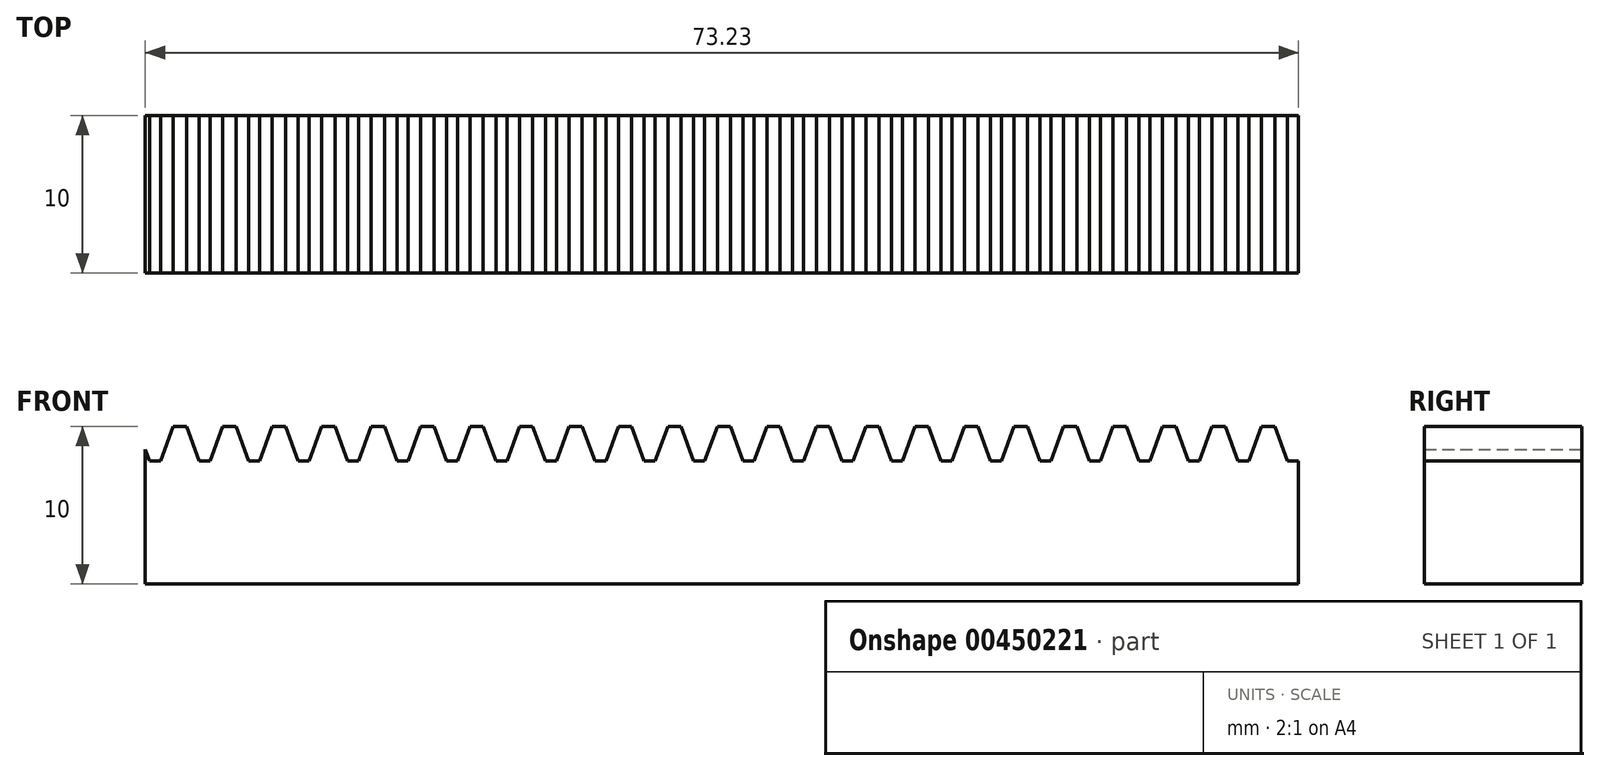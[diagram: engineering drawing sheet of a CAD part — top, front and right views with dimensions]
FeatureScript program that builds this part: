
annotation { "Feature Type Name" : "Feature", "Feature Type Description" : "" }
export const myFeature = defineFeature(function(context is Context, id is Id, definition is map)
    precondition{}
    {
        {
            var Q0;
            Q0=qCreatedBy(makeId("Front.planeOp"),FACE);
            var sketch = newSketch(context, id + "F0", { "sketchPlane" : qUnion([Q0])});
            skLineSegment(sketch, "E0", {"start": v(245.18, 2.55) * mm, "end": v(245.77, 2.55) * mm});
            skLineSegment(sketch, "E1", {"start": v(245.77, 2.55) * mm, "end": v(245.77, -5.25) * mm});
            skLineSegment(sketch, "E2", {"start": v(245.77, -5.25) * mm, "end": v(-50.4, -5.25) * mm});
            skLineSegment(sketch, "E3", {"start": v(244.38, 4.75) * mm, "end": v(245.18, 2.55) * mm});
            skLineSegment(sketch, "E4", {"start": v(242.74, 2.55) * mm, "end": v(243.54, 4.75) * mm});
            skLineSegment(sketch, "E5", {"start": v(242.04, 2.55) * mm, "end": v(242.74, 2.55) * mm});
            skLineSegment(sketch, "E6", {"start": v(243.54, 4.75) * mm, "end": v(244.38, 4.75) * mm});
            skLineSegment(sketch, "E7", {"start": v(241.24, 4.75) * mm, "end": v(242.04, 2.55) * mm});
            skLineSegment(sketch, "E8", {"start": v(240.4, 4.75) * mm, "end": v(241.24, 4.75) * mm});
            skLineSegment(sketch, "E9", {"start": v(239.6, 2.55) * mm, "end": v(240.4, 4.75) * mm});
            skLineSegment(sketch, "E10", {"start": v(238.9, 2.55) * mm, "end": v(239.6, 2.55) * mm});
            skLineSegment(sketch, "E11", {"start": v(238.1, 4.75) * mm, "end": v(238.9, 2.55) * mm});
            skLineSegment(sketch, "E12", {"start": v(237.25, 4.75) * mm, "end": v(238.1, 4.75) * mm});
            skLineSegment(sketch, "E13", {"start": v(236.45, 2.55) * mm, "end": v(237.25, 4.75) * mm});
            skLineSegment(sketch, "E14", {"start": v(235.76, 2.55) * mm, "end": v(236.45, 2.55) * mm});
            skLineSegment(sketch, "E15", {"start": v(234.96, 4.75) * mm, "end": v(235.76, 2.55) * mm});
            skLineSegment(sketch, "E16", {"start": v(234.11, 4.75) * mm, "end": v(234.96, 4.75) * mm});
            skLineSegment(sketch, "E17", {"start": v(233.31, 2.55) * mm, "end": v(234.11, 4.75) * mm});
            skLineSegment(sketch, "E18", {"start": v(232.62, 2.55) * mm, "end": v(233.31, 2.55) * mm});
            skLineSegment(sketch, "E19", {"start": v(231.81, 4.75) * mm, "end": v(232.62, 2.55) * mm});
            skLineSegment(sketch, "E20", {"start": v(230.97, 4.75) * mm, "end": v(231.81, 4.75) * mm});
            skLineSegment(sketch, "E21", {"start": v(230.17, 2.55) * mm, "end": v(230.97, 4.75) * mm});
            skLineSegment(sketch, "E22", {"start": v(229.47, 2.55) * mm, "end": v(230.17, 2.55) * mm});
            skLineSegment(sketch, "E23", {"start": v(228.67, 4.75) * mm, "end": v(229.47, 2.55) * mm});
            skLineSegment(sketch, "E24", {"start": v(227.83, 4.75) * mm, "end": v(228.67, 4.75) * mm});
            skLineSegment(sketch, "E25", {"start": v(227.03, 2.55) * mm, "end": v(227.83, 4.75) * mm});
            skLineSegment(sketch, "E26", {"start": v(226.33, 2.55) * mm, "end": v(227.03, 2.55) * mm});
            skLineSegment(sketch, "E27", {"start": v(225.53, 4.75) * mm, "end": v(226.33, 2.55) * mm});
            skLineSegment(sketch, "E28", {"start": v(224.69, 4.75) * mm, "end": v(225.53, 4.75) * mm});
            skLineSegment(sketch, "E29", {"start": v(223.89, 2.55) * mm, "end": v(224.69, 4.75) * mm});
            skLineSegment(sketch, "E30", {"start": v(223.2, 2.55) * mm, "end": v(223.89, 2.55) * mm});
            skLineSegment(sketch, "E31", {"start": v(222.39, 4.75) * mm, "end": v(223.2, 2.55) * mm});
            skLineSegment(sketch, "E32", {"start": v(221.55, 4.75) * mm, "end": v(222.39, 4.75) * mm});
            skLineSegment(sketch, "E33", {"start": v(220.75, 2.55) * mm, "end": v(221.55, 4.75) * mm});
            skLineSegment(sketch, "E34", {"start": v(220.05, 2.55) * mm, "end": v(220.75, 2.55) * mm});
            skLineSegment(sketch, "E35", {"start": v(219.25, 4.75) * mm, "end": v(220.05, 2.55) * mm});
            skLineSegment(sketch, "E36", {"start": v(218.4, 4.75) * mm, "end": v(219.25, 4.75) * mm});
            skLineSegment(sketch, "E37", {"start": v(217.6, 2.55) * mm, "end": v(218.4, 4.75) * mm});
            skLineSegment(sketch, "E38", {"start": v(216.9, 2.55) * mm, "end": v(217.6, 2.55) * mm});
            skLineSegment(sketch, "E39", {"start": v(216.1, 4.75) * mm, "end": v(216.9, 2.55) * mm});
            skLineSegment(sketch, "E40", {"start": v(215.26, 4.75) * mm, "end": v(216.1, 4.75) * mm});
            skLineSegment(sketch, "E41", {"start": v(214.46, 2.55) * mm, "end": v(215.26, 4.75) * mm});
            skLineSegment(sketch, "E42", {"start": v(213.77, 2.55) * mm, "end": v(214.46, 2.55) * mm});
            skLineSegment(sketch, "E43", {"start": v(212.96, 4.75) * mm, "end": v(213.77, 2.55) * mm});
            skLineSegment(sketch, "E44", {"start": v(212.12, 4.75) * mm, "end": v(212.96, 4.75) * mm});
            skLineSegment(sketch, "E45", {"start": v(211.32, 2.55) * mm, "end": v(212.12, 4.75) * mm});
            skLineSegment(sketch, "E46", {"start": v(210.62, 2.55) * mm, "end": v(211.32, 2.55) * mm});
            skLineSegment(sketch, "E47", {"start": v(209.82, 4.75) * mm, "end": v(210.62, 2.55) * mm});
            skLineSegment(sketch, "E48", {"start": v(208.98, 4.75) * mm, "end": v(209.82, 4.75) * mm});
            skLineSegment(sketch, "E49", {"start": v(208.18, 2.55) * mm, "end": v(208.98, 4.75) * mm});
            skLineSegment(sketch, "E50", {"start": v(207.48, 2.55) * mm, "end": v(208.18, 2.55) * mm});
            skLineSegment(sketch, "E51", {"start": v(206.68, 4.75) * mm, "end": v(207.48, 2.55) * mm});
            skLineSegment(sketch, "E52", {"start": v(205.84, 4.75) * mm, "end": v(206.68, 4.75) * mm});
            skLineSegment(sketch, "E53", {"start": v(205.04, 2.55) * mm, "end": v(205.84, 4.75) * mm});
            skLineSegment(sketch, "E54", {"start": v(204.34, 2.55) * mm, "end": v(205.04, 2.55) * mm});
            skLineSegment(sketch, "E55", {"start": v(203.54, 4.75) * mm, "end": v(204.34, 2.55) * mm});
            skLineSegment(sketch, "E56", {"start": v(202.7, 4.75) * mm, "end": v(203.54, 4.75) * mm});
            skLineSegment(sketch, "E57", {"start": v(201.9, 2.55) * mm, "end": v(202.7, 4.75) * mm});
            skLineSegment(sketch, "E58", {"start": v(201.2, 2.55) * mm, "end": v(201.9, 2.55) * mm});
            skLineSegment(sketch, "E59", {"start": v(200.4, 4.75) * mm, "end": v(201.2, 2.55) * mm});
            skLineSegment(sketch, "E60", {"start": v(199.56, 4.75) * mm, "end": v(200.4, 4.75) * mm});
            skLineSegment(sketch, "E61", {"start": v(198.75, 2.55) * mm, "end": v(199.56, 4.75) * mm});
            skLineSegment(sketch, "E62", {"start": v(198.06, 2.55) * mm, "end": v(198.75, 2.55) * mm});
            skLineSegment(sketch, "E63", {"start": v(197.26, 4.75) * mm, "end": v(198.06, 2.55) * mm});
            skLineSegment(sketch, "E64", {"start": v(196.41, 4.75) * mm, "end": v(197.26, 4.75) * mm});
            skLineSegment(sketch, "E65", {"start": v(195.61, 2.55) * mm, "end": v(196.41, 4.75) * mm});
            skLineSegment(sketch, "E66", {"start": v(194.92, 2.55) * mm, "end": v(195.61, 2.55) * mm});
            skLineSegment(sketch, "E67", {"start": v(194.12, 4.75) * mm, "end": v(194.92, 2.55) * mm});
            skLineSegment(sketch, "E68", {"start": v(193.27, 4.75) * mm, "end": v(194.12, 4.75) * mm});
            skLineSegment(sketch, "E69", {"start": v(192.47, 2.55) * mm, "end": v(193.27, 4.75) * mm});
            skLineSegment(sketch, "E70", {"start": v(191.77, 2.55) * mm, "end": v(192.47, 2.55) * mm});
            skLineSegment(sketch, "E71", {"start": v(190.97, 4.75) * mm, "end": v(191.77, 2.55) * mm});
            skLineSegment(sketch, "E72", {"start": v(190.13, 4.75) * mm, "end": v(190.97, 4.75) * mm});
            skLineSegment(sketch, "E73", {"start": v(189.33, 2.55) * mm, "end": v(190.13, 4.75) * mm});
            skLineSegment(sketch, "E74", {"start": v(188.63, 2.55) * mm, "end": v(189.33, 2.55) * mm});
            skLineSegment(sketch, "E75", {"start": v(187.83, 4.75) * mm, "end": v(188.63, 2.55) * mm});
            skLineSegment(sketch, "E76", {"start": v(186.99, 4.75) * mm, "end": v(187.83, 4.75) * mm});
            skLineSegment(sketch, "E77", {"start": v(186.19, 2.55) * mm, "end": v(186.99, 4.75) * mm});
            skLineSegment(sketch, "E78", {"start": v(185.5, 2.55) * mm, "end": v(186.19, 2.55) * mm});
            skLineSegment(sketch, "E79", {"start": v(184.7, 4.75) * mm, "end": v(185.5, 2.55) * mm});
            skLineSegment(sketch, "E80", {"start": v(183.85, 4.75) * mm, "end": v(184.7, 4.75) * mm});
            skLineSegment(sketch, "E81", {"start": v(183.05, 2.55) * mm, "end": v(183.85, 4.75) * mm});
            skLineSegment(sketch, "E82", {"start": v(182.35, 2.55) * mm, "end": v(183.05, 2.55) * mm});
            skLineSegment(sketch, "E83", {"start": v(181.55, 4.75) * mm, "end": v(182.35, 2.55) * mm});
            skLineSegment(sketch, "E84", {"start": v(180.7, 4.75) * mm, "end": v(181.55, 4.75) * mm});
            skLineSegment(sketch, "E85", {"start": v(179.9, 2.55) * mm, "end": v(180.7, 4.75) * mm});
            skLineSegment(sketch, "E86", {"start": v(179.2, 2.55) * mm, "end": v(179.9, 2.55) * mm});
            skLineSegment(sketch, "E87", {"start": v(178.4, 4.75) * mm, "end": v(179.2, 2.55) * mm});
            skLineSegment(sketch, "E88", {"start": v(177.56, 4.75) * mm, "end": v(178.4, 4.75) * mm});
            skLineSegment(sketch, "E89", {"start": v(176.76, 2.55) * mm, "end": v(177.56, 4.75) * mm});
            skLineSegment(sketch, "E90", {"start": v(176.07, 2.55) * mm, "end": v(176.76, 2.55) * mm});
            skLineSegment(sketch, "E91", {"start": v(175.27, 4.75) * mm, "end": v(176.07, 2.55) * mm});
            skLineSegment(sketch, "E92", {"start": v(174.42, 4.75) * mm, "end": v(175.27, 4.75) * mm});
            skLineSegment(sketch, "E93", {"start": v(173.62, 2.55) * mm, "end": v(174.42, 4.75) * mm});
            skLineSegment(sketch, "E94", {"start": v(172.93, 2.55) * mm, "end": v(173.62, 2.55) * mm});
            skLineSegment(sketch, "E95", {"start": v(172.12, 4.75) * mm, "end": v(172.93, 2.55) * mm});
            skLineSegment(sketch, "E96", {"start": v(171.28, 4.75) * mm, "end": v(172.12, 4.75) * mm});
            skLineSegment(sketch, "E97", {"start": v(170.48, 2.55) * mm, "end": v(171.28, 4.75) * mm});
            skLineSegment(sketch, "E98", {"start": v(169.78, 2.55) * mm, "end": v(170.48, 2.55) * mm});
            skLineSegment(sketch, "E99", {"start": v(168.98, 4.75) * mm, "end": v(169.78, 2.55) * mm});
            skLineSegment(sketch, "E100", {"start": v(168.14, 4.75) * mm, "end": v(168.98, 4.75) * mm});
            skLineSegment(sketch, "E101", {"start": v(167.34, 2.55) * mm, "end": v(168.14, 4.75) * mm});
            skLineSegment(sketch, "E102", {"start": v(166.64, 2.55) * mm, "end": v(167.34, 2.55) * mm});
            skLineSegment(sketch, "E103", {"start": v(165.84, 4.75) * mm, "end": v(166.64, 2.55) * mm});
            skLineSegment(sketch, "E104", {"start": v(165, 4.75) * mm, "end": v(165.84, 4.75) * mm});
            skLineSegment(sketch, "E105", {"start": v(164.2, 2.55) * mm, "end": v(165, 4.75) * mm});
            skLineSegment(sketch, "E106", {"start": v(163.5, 2.55) * mm, "end": v(164.2, 2.55) * mm});
            skLineSegment(sketch, "E107", {"start": v(162.7, 4.75) * mm, "end": v(163.5, 2.55) * mm});
            skLineSegment(sketch, "E108", {"start": v(161.86, 4.75) * mm, "end": v(162.7, 4.75) * mm});
            skLineSegment(sketch, "E109", {"start": v(161.06, 2.55) * mm, "end": v(161.86, 4.75) * mm});
            skLineSegment(sketch, "E110", {"start": v(160.36, 2.55) * mm, "end": v(161.06, 2.55) * mm});
            skLineSegment(sketch, "E111", {"start": v(159.56, 4.75) * mm, "end": v(160.36, 2.55) * mm});
            skLineSegment(sketch, "E112", {"start": v(158.72, 4.75) * mm, "end": v(159.56, 4.75) * mm});
            skLineSegment(sketch, "E113", {"start": v(157.91, 2.55) * mm, "end": v(158.72, 4.75) * mm});
            skLineSegment(sketch, "E114", {"start": v(157.22, 2.55) * mm, "end": v(157.91, 2.55) * mm});
            skLineSegment(sketch, "E115", {"start": v(156.42, 4.75) * mm, "end": v(157.22, 2.55) * mm});
            skLineSegment(sketch, "E116", {"start": v(155.57, 4.75) * mm, "end": v(156.42, 4.75) * mm});
            skLineSegment(sketch, "E117", {"start": v(154.77, 2.55) * mm, "end": v(155.57, 4.75) * mm});
            skLineSegment(sketch, "E118", {"start": v(154.08, 2.55) * mm, "end": v(154.77, 2.55) * mm});
            skLineSegment(sketch, "E119", {"start": v(153.27, 4.75) * mm, "end": v(154.08, 2.55) * mm});
            skLineSegment(sketch, "E120", {"start": v(152.43, 4.75) * mm, "end": v(153.27, 4.75) * mm});
            skLineSegment(sketch, "E121", {"start": v(151.63, 2.55) * mm, "end": v(152.43, 4.75) * mm});
            skLineSegment(sketch, "E122", {"start": v(150.93, 2.55) * mm, "end": v(151.63, 2.55) * mm});
            skLineSegment(sketch, "E123", {"start": v(150.13, 4.75) * mm, "end": v(150.93, 2.55) * mm});
            skLineSegment(sketch, "E124", {"start": v(149.3, 4.75) * mm, "end": v(150.13, 4.75) * mm});
            skLineSegment(sketch, "E125", {"start": v(148.49, 2.55) * mm, "end": v(149.3, 4.75) * mm});
            skLineSegment(sketch, "E126", {"start": v(147.8, 2.55) * mm, "end": v(148.49, 2.55) * mm});
            skLineSegment(sketch, "E127", {"start": v(147, 4.75) * mm, "end": v(147.8, 2.55) * mm});
            skLineSegment(sketch, "E128", {"start": v(146.15, 4.75) * mm, "end": v(147, 4.75) * mm});
            skLineSegment(sketch, "E129", {"start": v(145.35, 2.55) * mm, "end": v(146.15, 4.75) * mm});
            skLineSegment(sketch, "E130", {"start": v(144.65, 2.55) * mm, "end": v(145.35, 2.55) * mm});
            skLineSegment(sketch, "E131", {"start": v(143.85, 4.75) * mm, "end": v(144.65, 2.55) * mm});
            skLineSegment(sketch, "E132", {"start": v(143, 4.75) * mm, "end": v(143.85, 4.75) * mm});
            skLineSegment(sketch, "E133", {"start": v(142.2, 2.55) * mm, "end": v(143, 4.75) * mm});
            skLineSegment(sketch, "E134", {"start": v(141.5, 2.55) * mm, "end": v(142.2, 2.55) * mm});
            skLineSegment(sketch, "E135", {"start": v(140.7, 4.75) * mm, "end": v(141.5, 2.55) * mm});
            skLineSegment(sketch, "E136", {"start": v(139.87, 4.75) * mm, "end": v(140.7, 4.75) * mm});
            skLineSegment(sketch, "E137", {"start": v(139.06, 2.55) * mm, "end": v(139.87, 4.75) * mm});
            skLineSegment(sketch, "E138", {"start": v(138.37, 2.55) * mm, "end": v(139.06, 2.55) * mm});
            skLineSegment(sketch, "E139", {"start": v(137.57, 4.75) * mm, "end": v(138.37, 2.55) * mm});
            skLineSegment(sketch, "E140", {"start": v(136.72, 4.75) * mm, "end": v(137.57, 4.75) * mm});
            skLineSegment(sketch, "E141", {"start": v(135.92, 2.55) * mm, "end": v(136.72, 4.75) * mm});
            skLineSegment(sketch, "E142", {"start": v(135.23, 2.55) * mm, "end": v(135.92, 2.55) * mm});
            skLineSegment(sketch, "E143", {"start": v(134.43, 4.75) * mm, "end": v(135.23, 2.55) * mm});
            skLineSegment(sketch, "E144", {"start": v(133.58, 4.75) * mm, "end": v(134.43, 4.75) * mm});
            skLineSegment(sketch, "E145", {"start": v(132.78, 2.55) * mm, "end": v(133.58, 4.75) * mm});
            skLineSegment(sketch, "E146", {"start": v(132.08, 2.55) * mm, "end": v(132.78, 2.55) * mm});
            skLineSegment(sketch, "E147", {"start": v(131.28, 4.75) * mm, "end": v(132.08, 2.55) * mm});
            skLineSegment(sketch, "E148", {"start": v(130.44, 4.75) * mm, "end": v(131.28, 4.75) * mm});
            skLineSegment(sketch, "E149", {"start": v(129.64, 2.55) * mm, "end": v(130.44, 4.75) * mm});
            skLineSegment(sketch, "E150", {"start": v(128.94, 2.55) * mm, "end": v(129.64, 2.55) * mm});
            skLineSegment(sketch, "E151", {"start": v(128.14, 4.75) * mm, "end": v(128.94, 2.55) * mm});
            skLineSegment(sketch, "E152", {"start": v(127.3, 4.75) * mm, "end": v(128.14, 4.75) * mm});
            skLineSegment(sketch, "E153", {"start": v(126.5, 2.55) * mm, "end": v(127.3, 4.75) * mm});
            skLineSegment(sketch, "E154", {"start": v(125.8, 2.55) * mm, "end": v(126.5, 2.55) * mm});
            skLineSegment(sketch, "E155", {"start": v(125, 4.75) * mm, "end": v(125.8, 2.55) * mm});
            skLineSegment(sketch, "E156", {"start": v(124.16, 4.75) * mm, "end": v(125, 4.75) * mm});
            skLineSegment(sketch, "E157", {"start": v(123.36, 2.55) * mm, "end": v(124.16, 4.75) * mm});
            skLineSegment(sketch, "E158", {"start": v(122.66, 2.55) * mm, "end": v(123.36, 2.55) * mm});
            skLineSegment(sketch, "E159", {"start": v(121.86, 4.75) * mm, "end": v(122.66, 2.55) * mm});
            skLineSegment(sketch, "E160", {"start": v(121.02, 4.75) * mm, "end": v(121.86, 4.75) * mm});
            skLineSegment(sketch, "E161", {"start": v(120.22, 2.55) * mm, "end": v(121.02, 4.75) * mm});
            skLineSegment(sketch, "E162", {"start": v(119.52, 2.55) * mm, "end": v(120.22, 2.55) * mm});
            skLineSegment(sketch, "E163", {"start": v(118.72, 4.75) * mm, "end": v(119.52, 2.55) * mm});
            skLineSegment(sketch, "E164", {"start": v(117.87, 4.75) * mm, "end": v(118.72, 4.75) * mm});
            skLineSegment(sketch, "E165", {"start": v(117.07, 2.55) * mm, "end": v(117.87, 4.75) * mm});
            skLineSegment(sketch, "E166", {"start": v(116.38, 2.55) * mm, "end": v(117.07, 2.55) * mm});
            skLineSegment(sketch, "E167", {"start": v(115.58, 4.75) * mm, "end": v(116.38, 2.55) * mm});
            skLineSegment(sketch, "E168", {"start": v(114.73, 4.75) * mm, "end": v(115.58, 4.75) * mm});
            skLineSegment(sketch, "E169", {"start": v(113.93, 2.55) * mm, "end": v(114.73, 4.75) * mm});
            skLineSegment(sketch, "E170", {"start": v(113.23, 2.55) * mm, "end": v(113.93, 2.55) * mm});
            skLineSegment(sketch, "E171", {"start": v(112.43, 4.75) * mm, "end": v(113.23, 2.55) * mm});
            skLineSegment(sketch, "E172", {"start": v(111.6, 4.75) * mm, "end": v(112.43, 4.75) * mm});
            skLineSegment(sketch, "E173", {"start": v(110.8, 2.55) * mm, "end": v(111.6, 4.75) * mm});
            skLineSegment(sketch, "E174", {"start": v(110.1, 2.55) * mm, "end": v(110.8, 2.55) * mm});
            skLineSegment(sketch, "E175", {"start": v(109.3, 4.75) * mm, "end": v(110.1, 2.55) * mm});
            skLineSegment(sketch, "E176", {"start": v(108.45, 4.75) * mm, "end": v(109.3, 4.75) * mm});
            skLineSegment(sketch, "E177", {"start": v(107.65, 2.55) * mm, "end": v(108.45, 4.75) * mm});
            skLineSegment(sketch, "E178", {"start": v(106.95, 2.55) * mm, "end": v(107.65, 2.55) * mm});
            skLineSegment(sketch, "E179", {"start": v(106.15, 4.75) * mm, "end": v(106.95, 2.55) * mm});
            skLineSegment(sketch, "E180", {"start": v(105.3, 4.75) * mm, "end": v(106.15, 4.75) * mm});
            skLineSegment(sketch, "E181", {"start": v(104.5, 2.55) * mm, "end": v(105.3, 4.75) * mm});
            skLineSegment(sketch, "E182", {"start": v(103.81, 2.55) * mm, "end": v(104.5, 2.55) * mm});
            skLineSegment(sketch, "E183", {"start": v(103, 4.75) * mm, "end": v(103.81, 2.55) * mm});
            skLineSegment(sketch, "E184", {"start": v(102.17, 4.75) * mm, "end": v(103, 4.75) * mm});
            skLineSegment(sketch, "E185", {"start": v(101.37, 2.55) * mm, "end": v(102.17, 4.75) * mm});
            skLineSegment(sketch, "E186", {"start": v(100.67, 2.55) * mm, "end": v(101.37, 2.55) * mm});
            skLineSegment(sketch, "E187", {"start": v(99.87, 4.75) * mm, "end": v(100.67, 2.55) * mm});
            skLineSegment(sketch, "E188", {"start": v(99.02, 4.75) * mm, "end": v(99.87, 4.75) * mm});
            skLineSegment(sketch, "E189", {"start": v(98.22, 2.55) * mm, "end": v(99.02, 4.75) * mm});
            skLineSegment(sketch, "E190", {"start": v(97.53, 2.55) * mm, "end": v(98.22, 2.55) * mm});
            skLineSegment(sketch, "E191", {"start": v(96.73, 4.75) * mm, "end": v(97.53, 2.55) * mm});
            skLineSegment(sketch, "E192", {"start": v(95.88, 4.75) * mm, "end": v(96.73, 4.75) * mm});
            skLineSegment(sketch, "E193", {"start": v(95.08, 2.55) * mm, "end": v(95.88, 4.75) * mm});
            skLineSegment(sketch, "E194", {"start": v(94.39, 2.55) * mm, "end": v(95.08, 2.55) * mm});
            skLineSegment(sketch, "E195", {"start": v(93.58, 4.75) * mm, "end": v(94.39, 2.55) * mm});
            skLineSegment(sketch, "E196", {"start": v(92.74, 4.75) * mm, "end": v(93.58, 4.75) * mm});
            skLineSegment(sketch, "E197", {"start": v(91.94, 2.55) * mm, "end": v(92.74, 4.75) * mm});
            skLineSegment(sketch, "E198", {"start": v(91.24, 2.55) * mm, "end": v(91.94, 2.55) * mm});
            skLineSegment(sketch, "E199", {"start": v(90.44, 4.75) * mm, "end": v(91.24, 2.55) * mm});
            skLineSegment(sketch, "E200", {"start": v(89.6, 4.75) * mm, "end": v(90.44, 4.75) * mm});
            skLineSegment(sketch, "E201", {"start": v(88.8, 2.55) * mm, "end": v(89.6, 4.75) * mm});
            skLineSegment(sketch, "E202", {"start": v(88.1, 2.55) * mm, "end": v(88.8, 2.55) * mm});
            skLineSegment(sketch, "E203", {"start": v(87.3, 4.75) * mm, "end": v(88.1, 2.55) * mm});
            skLineSegment(sketch, "E204", {"start": v(86.46, 4.75) * mm, "end": v(87.3, 4.75) * mm});
            skLineSegment(sketch, "E205", {"start": v(85.66, 2.55) * mm, "end": v(86.46, 4.75) * mm});
            skLineSegment(sketch, "E206", {"start": v(84.96, 2.55) * mm, "end": v(85.66, 2.55) * mm});
            skLineSegment(sketch, "E207", {"start": v(84.16, 4.75) * mm, "end": v(84.96, 2.55) * mm});
            skLineSegment(sketch, "E208", {"start": v(83.32, 4.75) * mm, "end": v(84.16, 4.75) * mm});
            skLineSegment(sketch, "E209", {"start": v(82.52, 2.55) * mm, "end": v(83.32, 4.75) * mm});
            skLineSegment(sketch, "E210", {"start": v(81.82, 2.55) * mm, "end": v(82.52, 2.55) * mm});
            skLineSegment(sketch, "E211", {"start": v(81.02, 4.75) * mm, "end": v(81.82, 2.55) * mm});
            skLineSegment(sketch, "E212", {"start": v(80.18, 4.75) * mm, "end": v(81.02, 4.75) * mm});
            skLineSegment(sketch, "E213", {"start": v(79.37, 2.55) * mm, "end": v(80.18, 4.75) * mm});
            skLineSegment(sketch, "E214", {"start": v(78.68, 2.55) * mm, "end": v(79.37, 2.55) * mm});
            skLineSegment(sketch, "E215", {"start": v(77.88, 4.75) * mm, "end": v(78.68, 2.55) * mm});
            skLineSegment(sketch, "E216", {"start": v(77.03, 4.75) * mm, "end": v(77.88, 4.75) * mm});
            skLineSegment(sketch, "E217", {"start": v(76.23, 2.55) * mm, "end": v(77.03, 4.75) * mm});
            skLineSegment(sketch, "E218", {"start": v(75.54, 2.55) * mm, "end": v(76.23, 2.55) * mm});
            skLineSegment(sketch, "E219", {"start": v(74.73, 4.75) * mm, "end": v(75.54, 2.55) * mm});
            skLineSegment(sketch, "E220", {"start": v(73.9, 4.75) * mm, "end": v(74.73, 4.75) * mm});
            skLineSegment(sketch, "E221", {"start": v(73.1, 2.55) * mm, "end": v(73.9, 4.75) * mm});
            skLineSegment(sketch, "E222", {"start": v(72.4, 2.55) * mm, "end": v(73.1, 2.55) * mm});
            skLineSegment(sketch, "E223", {"start": v(71.6, 4.75) * mm, "end": v(72.4, 2.55) * mm});
            skLineSegment(sketch, "E224", {"start": v(70.75, 4.75) * mm, "end": v(71.6, 4.75) * mm});
            skLineSegment(sketch, "E225", {"start": v(69.95, 2.55) * mm, "end": v(70.75, 4.75) * mm});
            skLineSegment(sketch, "E226", {"start": v(69.25, 2.55) * mm, "end": v(69.95, 2.55) * mm});
            skLineSegment(sketch, "E227", {"start": v(68.45, 4.75) * mm, "end": v(69.25, 2.55) * mm});
            skLineSegment(sketch, "E228", {"start": v(67.6, 4.75) * mm, "end": v(68.45, 4.75) * mm});
            skLineSegment(sketch, "E229", {"start": v(66.8, 2.55) * mm, "end": v(67.6, 4.75) * mm});
            skLineSegment(sketch, "E230", {"start": v(66.11, 2.55) * mm, "end": v(66.8, 2.55) * mm});
            skLineSegment(sketch, "E231", {"start": v(65.31, 4.75) * mm, "end": v(66.11, 2.55) * mm});
            skLineSegment(sketch, "E232", {"start": v(64.47, 4.75) * mm, "end": v(65.31, 4.75) * mm});
            skLineSegment(sketch, "E233", {"start": v(63.67, 2.55) * mm, "end": v(64.47, 4.75) * mm});
            skLineSegment(sketch, "E234", {"start": v(62.97, 2.55) * mm, "end": v(63.67, 2.55) * mm});
            skLineSegment(sketch, "E235", {"start": v(62.17, 4.75) * mm, "end": v(62.97, 2.55) * mm});
            skLineSegment(sketch, "E236", {"start": v(61.33, 4.75) * mm, "end": v(62.17, 4.75) * mm});
            skLineSegment(sketch, "E237", {"start": v(60.53, 2.55) * mm, "end": v(61.33, 4.75) * mm});
            skLineSegment(sketch, "E238", {"start": v(59.83, 2.55) * mm, "end": v(60.53, 2.55) * mm});
            skLineSegment(sketch, "E239", {"start": v(59.03, 4.75) * mm, "end": v(59.83, 2.55) * mm});
            skLineSegment(sketch, "E240", {"start": v(58.18, 4.75) * mm, "end": v(59.03, 4.75) * mm});
            skLineSegment(sketch, "E241", {"start": v(57.38, 2.55) * mm, "end": v(58.18, 4.75) * mm});
            skLineSegment(sketch, "E242", {"start": v(56.69, 2.55) * mm, "end": v(57.38, 2.55) * mm});
            skLineSegment(sketch, "E243", {"start": v(55.89, 4.75) * mm, "end": v(56.69, 2.55) * mm});
            skLineSegment(sketch, "E244", {"start": v(55.04, 4.75) * mm, "end": v(55.89, 4.75) * mm});
            skLineSegment(sketch, "E245", {"start": v(54.24, 2.55) * mm, "end": v(55.04, 4.75) * mm});
            skLineSegment(sketch, "E246", {"start": v(53.54, 2.55) * mm, "end": v(54.24, 2.55) * mm});
            skLineSegment(sketch, "E247", {"start": v(52.74, 4.75) * mm, "end": v(53.54, 2.55) * mm});
            skLineSegment(sketch, "E248", {"start": v(51.9, 4.75) * mm, "end": v(52.74, 4.75) * mm});
            skLineSegment(sketch, "E249", {"start": v(51.1, 2.55) * mm, "end": v(51.9, 4.75) * mm});
            skLineSegment(sketch, "E250", {"start": v(50.4, 2.55) * mm, "end": v(51.1, 2.55) * mm});
            skLineSegment(sketch, "E251", {"start": v(49.6, 4.75) * mm, "end": v(50.4, 2.55) * mm});
            skLineSegment(sketch, "E252", {"start": v(48.76, 4.75) * mm, "end": v(49.6, 4.75) * mm});
            skLineSegment(sketch, "E253", {"start": v(47.96, 2.55) * mm, "end": v(48.76, 4.75) * mm});
            skLineSegment(sketch, "E254", {"start": v(47.26, 2.55) * mm, "end": v(47.96, 2.55) * mm});
            skLineSegment(sketch, "E255", {"start": v(46.46, 4.75) * mm, "end": v(47.26, 2.55) * mm});
            skLineSegment(sketch, "E256", {"start": v(45.62, 4.75) * mm, "end": v(46.46, 4.75) * mm});
            skLineSegment(sketch, "E257", {"start": v(44.82, 2.55) * mm, "end": v(45.62, 4.75) * mm});
            skLineSegment(sketch, "E258", {"start": v(44.12, 2.55) * mm, "end": v(44.82, 2.55) * mm});
            skLineSegment(sketch, "E259", {"start": v(43.32, 4.75) * mm, "end": v(44.12, 2.55) * mm});
            skLineSegment(sketch, "E260", {"start": v(42.48, 4.75) * mm, "end": v(43.32, 4.75) * mm});
            skLineSegment(sketch, "E261", {"start": v(41.68, 2.55) * mm, "end": v(42.48, 4.75) * mm});
            skLineSegment(sketch, "E262", {"start": v(40.98, 2.55) * mm, "end": v(41.68, 2.55) * mm});
            skLineSegment(sketch, "E263", {"start": v(40.18, 4.75) * mm, "end": v(40.98, 2.55) * mm});
            skLineSegment(sketch, "E264", {"start": v(39.33, 4.75) * mm, "end": v(40.18, 4.75) * mm});
            skLineSegment(sketch, "E265", {"start": v(38.53, 2.55) * mm, "end": v(39.33, 4.75) * mm});
            skLineSegment(sketch, "E266", {"start": v(37.84, 2.55) * mm, "end": v(38.53, 2.55) * mm});
            skLineSegment(sketch, "E267", {"start": v(37.04, 4.75) * mm, "end": v(37.84, 2.55) * mm});
            skLineSegment(sketch, "E268", {"start": v(36.2, 4.75) * mm, "end": v(37.04, 4.75) * mm});
            skLineSegment(sketch, "E269", {"start": v(35.4, 2.55) * mm, "end": v(36.2, 4.75) * mm});
            skLineSegment(sketch, "E270", {"start": v(34.7, 2.55) * mm, "end": v(35.4, 2.55) * mm});
            skLineSegment(sketch, "E271", {"start": v(33.9, 4.75) * mm, "end": v(34.7, 2.55) * mm});
            skLineSegment(sketch, "E272", {"start": v(33.05, 4.75) * mm, "end": v(33.9, 4.75) * mm});
            skLineSegment(sketch, "E273", {"start": v(32.25, 2.55) * mm, "end": v(33.05, 4.75) * mm});
            skLineSegment(sketch, "E274", {"start": v(31.55, 2.55) * mm, "end": v(32.25, 2.55) * mm});
            skLineSegment(sketch, "E275", {"start": v(30.75, 4.75) * mm, "end": v(31.55, 2.55) * mm});
            skLineSegment(sketch, "E276", {"start": v(29.9, 4.75) * mm, "end": v(30.75, 4.75) * mm});
            skLineSegment(sketch, "E277", {"start": v(29.1, 2.55) * mm, "end": v(29.9, 4.75) * mm});
            skLineSegment(sketch, "E278", {"start": v(28.41, 2.55) * mm, "end": v(29.1, 2.55) * mm});
            skLineSegment(sketch, "E279", {"start": v(27.61, 4.75) * mm, "end": v(28.41, 2.55) * mm});
            skLineSegment(sketch, "E280", {"start": v(26.77, 4.75) * mm, "end": v(27.61, 4.75) * mm});
            skLineSegment(sketch, "E281", {"start": v(25.97, 2.55) * mm, "end": v(26.77, 4.75) * mm});
            skLineSegment(sketch, "E282", {"start": v(25.27, 2.55) * mm, "end": v(25.97, 2.55) * mm});
            skLineSegment(sketch, "E283", {"start": v(24.47, 4.75) * mm, "end": v(25.27, 2.55) * mm});
            skLineSegment(sketch, "E284", {"start": v(23.63, 4.75) * mm, "end": v(24.47, 4.75) * mm});
            skLineSegment(sketch, "E285", {"start": v(22.83, 2.55) * mm, "end": v(23.63, 4.75) * mm});
            skLineSegment(sketch, "E286", {"start": v(22.13, 2.55) * mm, "end": v(22.83, 2.55) * mm});
            skLineSegment(sketch, "E287", {"start": v(21.33, 4.75) * mm, "end": v(22.13, 2.55) * mm});
            skLineSegment(sketch, "E288", {"start": v(20.49, 4.75) * mm, "end": v(21.33, 4.75) * mm});
            skLineSegment(sketch, "E289", {"start": v(19.68, 2.55) * mm, "end": v(20.49, 4.75) * mm});
            skLineSegment(sketch, "E290", {"start": v(18.99, 2.55) * mm, "end": v(19.68, 2.55) * mm});
            skLineSegment(sketch, "E291", {"start": v(18.19, 4.75) * mm, "end": v(18.99, 2.55) * mm});
            skLineSegment(sketch, "E292", {"start": v(17.34, 4.75) * mm, "end": v(18.19, 4.75) * mm});
            skLineSegment(sketch, "E293", {"start": v(16.54, 2.55) * mm, "end": v(17.34, 4.75) * mm});
            skLineSegment(sketch, "E294", {"start": v(15.85, 2.55) * mm, "end": v(16.54, 2.55) * mm});
            skLineSegment(sketch, "E295", {"start": v(15.04, 4.75) * mm, "end": v(15.85, 2.55) * mm});
            skLineSegment(sketch, "E296", {"start": v(14.2, 4.75) * mm, "end": v(15.04, 4.75) * mm});
            skLineSegment(sketch, "E297", {"start": v(13.4, 2.55) * mm, "end": v(14.2, 4.75) * mm});
            skLineSegment(sketch, "E298", {"start": v(12.7, 2.55) * mm, "end": v(13.4, 2.55) * mm});
            skLineSegment(sketch, "E299", {"start": v(11.9, 4.75) * mm, "end": v(12.7, 2.55) * mm});
            skLineSegment(sketch, "E300", {"start": v(11.06, 4.75) * mm, "end": v(11.9, 4.75) * mm});
            skLineSegment(sketch, "E301", {"start": v(10.26, 2.55) * mm, "end": v(11.06, 4.75) * mm});
            skLineSegment(sketch, "E302", {"start": v(9.56, 2.55) * mm, "end": v(10.26, 2.55) * mm});
            skLineSegment(sketch, "E303", {"start": v(8.76, 4.75) * mm, "end": v(9.56, 2.55) * mm});
            skLineSegment(sketch, "E304", {"start": v(7.92, 4.75) * mm, "end": v(8.76, 4.75) * mm});
            skLineSegment(sketch, "E305", {"start": v(7.12, 2.55) * mm, "end": v(7.92, 4.75) * mm});
            skLineSegment(sketch, "E306", {"start": v(6.42, 2.55) * mm, "end": v(7.12, 2.55) * mm});
            skLineSegment(sketch, "E307", {"start": v(5.62, 4.75) * mm, "end": v(6.42, 2.55) * mm});
            skLineSegment(sketch, "E308", {"start": v(4.78, 4.75) * mm, "end": v(5.62, 4.75) * mm});
            skLineSegment(sketch, "E309", {"start": v(3.98, 2.55) * mm, "end": v(4.78, 4.75) * mm});
            skLineSegment(sketch, "E310", {"start": v(3.28, 2.55) * mm, "end": v(3.98, 2.55) * mm});
            skLineSegment(sketch, "E311", {"start": v(2.48, 4.75) * mm, "end": v(3.28, 2.55) * mm});
            skLineSegment(sketch, "E312", {"start": v(1.64, 4.75) * mm, "end": v(2.48, 4.75) * mm});
            skLineSegment(sketch, "E313", {"start": v(0.83, 2.55) * mm, "end": v(1.64, 4.75) * mm});
            skLineSegment(sketch, "E314", {"start": v(0.14, 2.55) * mm, "end": v(0.83, 2.55) * mm});
            skLineSegment(sketch, "E315", {"start": v(-0.66, 4.75) * mm, "end": v(0.14, 2.55) * mm});
            skLineSegment(sketch, "E316", {"start": v(-1.5, 4.75) * mm, "end": v(-0.66, 4.75) * mm});
            skLineSegment(sketch, "E317", {"start": v(-2.3, 2.55) * mm, "end": v(-1.5, 4.75) * mm});
            skLineSegment(sketch, "E318", {"start": v(-3, 2.55) * mm, "end": v(-2.3, 2.55) * mm});
            skLineSegment(sketch, "E319", {"start": v(-3.8, 4.75) * mm, "end": v(-3, 2.55) * mm});
            skLineSegment(sketch, "E320", {"start": v(-4.65, 4.75) * mm, "end": v(-3.8, 4.75) * mm});
            skLineSegment(sketch, "E321", {"start": v(-5.45, 2.55) * mm, "end": v(-4.65, 4.75) * mm});
            skLineSegment(sketch, "E322", {"start": v(-6.15, 2.55) * mm, "end": v(-5.45, 2.55) * mm});
            skLineSegment(sketch, "E323", {"start": v(-6.95, 4.75) * mm, "end": v(-6.15, 2.55) * mm});
            skLineSegment(sketch, "E324", {"start": v(-7.79, 4.75) * mm, "end": v(-6.95, 4.75) * mm});
            skLineSegment(sketch, "E325", {"start": v(-8.59, 2.55) * mm, "end": v(-7.79, 4.75) * mm});
            skLineSegment(sketch, "E326", {"start": v(-9.29, 2.55) * mm, "end": v(-8.59, 2.55) * mm});
            skLineSegment(sketch, "E327", {"start": v(-10.09, 4.75) * mm, "end": v(-9.29, 2.55) * mm});
            skLineSegment(sketch, "E328", {"start": v(-10.93, 4.75) * mm, "end": v(-10.09, 4.75) * mm});
            skLineSegment(sketch, "E329", {"start": v(-11.73, 2.55) * mm, "end": v(-10.93, 4.75) * mm});
            skLineSegment(sketch, "E330", {"start": v(-12.43, 2.55) * mm, "end": v(-11.73, 2.55) * mm});
            skLineSegment(sketch, "E331", {"start": v(-13.23, 4.75) * mm, "end": v(-12.43, 2.55) * mm});
            skLineSegment(sketch, "E332", {"start": v(-14.07, 4.75) * mm, "end": v(-13.23, 4.75) * mm});
            skLineSegment(sketch, "E333", {"start": v(-14.87, 2.55) * mm, "end": v(-14.07, 4.75) * mm});
            skLineSegment(sketch, "E334", {"start": v(-15.57, 2.55) * mm, "end": v(-14.87, 2.55) * mm});
            skLineSegment(sketch, "E335", {"start": v(-16.37, 4.75) * mm, "end": v(-15.57, 2.55) * mm});
            skLineSegment(sketch, "E336", {"start": v(-17.21, 4.75) * mm, "end": v(-16.37, 4.75) * mm});
            skLineSegment(sketch, "E337", {"start": v(-18.01, 2.55) * mm, "end": v(-17.21, 4.75) * mm});
            skLineSegment(sketch, "E338", {"start": v(-18.71, 2.55) * mm, "end": v(-18.01, 2.55) * mm});
            skLineSegment(sketch, "E339", {"start": v(-19.51, 4.75) * mm, "end": v(-18.71, 2.55) * mm});
            skLineSegment(sketch, "E340", {"start": v(-20.36, 4.75) * mm, "end": v(-19.51, 4.75) * mm});
            skLineSegment(sketch, "E341", {"start": v(-21.16, 2.55) * mm, "end": v(-20.36, 4.75) * mm});
            skLineSegment(sketch, "E342", {"start": v(-21.85, 2.55) * mm, "end": v(-21.16, 2.55) * mm});
            skLineSegment(sketch, "E343", {"start": v(-22.65, 4.75) * mm, "end": v(-21.85, 2.55) * mm});
            skLineSegment(sketch, "E344", {"start": v(-23.5, 4.75) * mm, "end": v(-22.65, 4.75) * mm});
            skLineSegment(sketch, "E345", {"start": v(-24.3, 2.55) * mm, "end": v(-23.5, 4.75) * mm});
            skLineSegment(sketch, "E346", {"start": v(-25, 2.55) * mm, "end": v(-24.3, 2.55) * mm});
            skLineSegment(sketch, "E347", {"start": v(-25.8, 4.75) * mm, "end": v(-25, 2.55) * mm});
            skLineSegment(sketch, "E348", {"start": v(-26.64, 4.75) * mm, "end": v(-25.8, 4.75) * mm});
            skLineSegment(sketch, "E349", {"start": v(-27.44, 2.55) * mm, "end": v(-26.64, 4.75) * mm});
            skLineSegment(sketch, "E350", {"start": v(-28.14, 2.55) * mm, "end": v(-27.44, 2.55) * mm});
            skLineSegment(sketch, "E351", {"start": v(-28.94, 4.75) * mm, "end": v(-28.14, 2.55) * mm});
            skLineSegment(sketch, "E352", {"start": v(-29.78, 4.75) * mm, "end": v(-28.94, 4.75) * mm});
            skLineSegment(sketch, "E353", {"start": v(-30.58, 2.55) * mm, "end": v(-29.78, 4.75) * mm});
            skLineSegment(sketch, "E354", {"start": v(-31.28, 2.55) * mm, "end": v(-30.58, 2.55) * mm});
            skLineSegment(sketch, "E355", {"start": v(-32.08, 4.75) * mm, "end": v(-31.28, 2.55) * mm});
            skLineSegment(sketch, "E356", {"start": v(-32.92, 4.75) * mm, "end": v(-32.08, 4.75) * mm});
            skLineSegment(sketch, "E357", {"start": v(-33.72, 2.55) * mm, "end": v(-32.92, 4.75) * mm});
            skLineSegment(sketch, "E358", {"start": v(-34.42, 2.55) * mm, "end": v(-33.72, 2.55) * mm});
            skLineSegment(sketch, "E359", {"start": v(-35.22, 4.75) * mm, "end": v(-34.42, 2.55) * mm});
            skLineSegment(sketch, "E360", {"start": v(-36.06, 4.75) * mm, "end": v(-35.22, 4.75) * mm});
            skLineSegment(sketch, "E361", {"start": v(-36.86, 2.55) * mm, "end": v(-36.06, 4.75) * mm});
            skLineSegment(sketch, "E362", {"start": v(-37.56, 2.55) * mm, "end": v(-36.86, 2.55) * mm});
            skLineSegment(sketch, "E363", {"start": v(-38.36, 4.75) * mm, "end": v(-37.56, 2.55) * mm});
            skLineSegment(sketch, "E364", {"start": v(-39.2, 4.75) * mm, "end": v(-38.36, 4.75) * mm});
            skLineSegment(sketch, "E365", {"start": v(-40, 2.55) * mm, "end": v(-39.2, 4.75) * mm});
            skLineSegment(sketch, "E366", {"start": v(-40.7, 2.55) * mm, "end": v(-40, 2.55) * mm});
            skLineSegment(sketch, "E367", {"start": v(-41.5, 4.75) * mm, "end": v(-40.7, 2.55) * mm});
            skLineSegment(sketch, "E368", {"start": v(-42.35, 4.75) * mm, "end": v(-41.5, 4.75) * mm});
            skLineSegment(sketch, "E369", {"start": v(-43.15, 2.55) * mm, "end": v(-42.35, 4.75) * mm});
            skLineSegment(sketch, "E370", {"start": v(-43.84, 2.55) * mm, "end": v(-43.15, 2.55) * mm});
            skLineSegment(sketch, "E371", {"start": v(-44.65, 4.75) * mm, "end": v(-43.84, 2.55) * mm});
            skLineSegment(sketch, "E372", {"start": v(-45.49, 4.75) * mm, "end": v(-44.65, 4.75) * mm});
            skLineSegment(sketch, "E373", {"start": v(-46.29, 2.55) * mm, "end": v(-45.49, 4.75) * mm});
            skLineSegment(sketch, "E374", {"start": v(-46.99, 2.55) * mm, "end": v(-46.29, 2.55) * mm});
            skLineSegment(sketch, "E375", {"start": v(-47.79, 4.75) * mm, "end": v(-46.99, 2.55) * mm});
            skLineSegment(sketch, "E376", {"start": v(-48.63, 4.75) * mm, "end": v(-47.79, 4.75) * mm});
            skLineSegment(sketch, "E377", {"start": v(-49.43, 2.55) * mm, "end": v(-48.63, 4.75) * mm});
            skLineSegment(sketch, "E378", {"start": v(-50.13, 2.55) * mm, "end": v(-49.43, 2.55) * mm});
            skLineSegment(sketch, "E379", {"start": v(-50.93, 4.75) * mm, "end": v(-50.13, 2.55) * mm});
            skLineSegment(sketch, "E380", {"start": v(-51.77, 4.75) * mm, "end": v(-50.93, 4.75) * mm});
            skLineSegment(sketch, "E381", {"start": v(-52.57, 2.55) * mm, "end": v(-51.77, 4.75) * mm});
            skLineSegment(sketch, "E382", {"start": v(-53.27, 2.55) * mm, "end": v(-52.57, 2.55) * mm});
            skLineSegment(sketch, "E383", {"start": v(-54.07, 4.75) * mm, "end": v(-53.27, 2.55) * mm});
            skLineSegment(sketch, "E384", {"start": v(-54.91, 4.75) * mm, "end": v(-54.07, 4.75) * mm});
            skLineSegment(sketch, "E385", {"start": v(-55.71, 2.55) * mm, "end": v(-54.91, 4.75) * mm});
            skLineSegment(sketch, "E386", {"start": v(-56.41, 2.55) * mm, "end": v(-55.71, 2.55) * mm});
            skLineSegment(sketch, "E387", {"start": v(-57.21, 4.75) * mm, "end": v(-56.41, 2.55) * mm});
            skLineSegment(sketch, "E388", {"start": v(-58.05, 4.75) * mm, "end": v(-57.21, 4.75) * mm});
            skLineSegment(sketch, "E389", {"start": v(-58.86, 2.55) * mm, "end": v(-58.05, 4.75) * mm});
            skLineSegment(sketch, "E390", {"start": v(-59.55, 2.55) * mm, "end": v(-58.86, 2.55) * mm});
            skLineSegment(sketch, "E391", {"start": v(-60.35, 4.75) * mm, "end": v(-59.55, 2.55) * mm});
            skLineSegment(sketch, "E392", {"start": v(-61.2, 4.75) * mm, "end": v(-60.35, 4.75) * mm});
            skLineSegment(sketch, "E393", {"start": v(-62, 2.55) * mm, "end": v(-61.2, 4.75) * mm});
            skLineSegment(sketch, "E394", {"start": v(-62.7, 2.55) * mm, "end": v(-62, 2.55) * mm});
            skLineSegment(sketch, "E395", {"start": v(-63.5, 4.75) * mm, "end": v(-62.7, 2.55) * mm});
            skLineSegment(sketch, "E396", {"start": v(-64.34, 4.75) * mm, "end": v(-63.5, 4.75) * mm});
            skLineSegment(sketch, "E397", {"start": v(-65.14, 2.55) * mm, "end": v(-64.34, 4.75) * mm});
            skLineSegment(sketch, "E398", {"start": v(-65.84, 2.55) * mm, "end": v(-65.14, 2.55) * mm});
            skLineSegment(sketch, "E399", {"start": v(-66.64, 4.75) * mm, "end": v(-65.84, 2.55) * mm});
            skLineSegment(sketch, "E400", {"start": v(-67.48, 4.75) * mm, "end": v(-66.64, 4.75) * mm});
            skLineSegment(sketch, "E401", {"start": v(-68.28, 2.55) * mm, "end": v(-67.48, 4.75) * mm});
            skLineSegment(sketch, "E402", {"start": v(-68.98, 2.55) * mm, "end": v(-68.28, 2.55) * mm});
            skLineSegment(sketch, "E403", {"start": v(-69.78, 4.75) * mm, "end": v(-68.98, 2.55) * mm});
            skLineSegment(sketch, "E404", {"start": v(-70.62, 4.75) * mm, "end": v(-69.78, 4.75) * mm});
            skLineSegment(sketch, "E405", {"start": v(-71.42, 2.55) * mm, "end": v(-70.62, 4.75) * mm});
            skLineSegment(sketch, "E406", {"start": v(-72.12, 2.55) * mm, "end": v(-71.42, 2.55) * mm});
            skLineSegment(sketch, "E407", {"start": v(-72.92, 4.75) * mm, "end": v(-72.12, 2.55) * mm});
            skLineSegment(sketch, "E408", {"start": v(-73.76, 4.75) * mm, "end": v(-72.92, 4.75) * mm});
            skLineSegment(sketch, "E409", {"start": v(-74.56, 2.55) * mm, "end": v(-73.76, 4.75) * mm});
            skLineSegment(sketch, "E410", {"start": v(-75.26, 2.55) * mm, "end": v(-74.56, 2.55) * mm});
            skLineSegment(sketch, "E411", {"start": v(-76.06, 4.75) * mm, "end": v(-75.26, 2.55) * mm});
            skLineSegment(sketch, "E412", {"start": v(-76.9, 4.75) * mm, "end": v(-76.06, 4.75) * mm});
            skLineSegment(sketch, "E413", {"start": v(-77.7, 2.55) * mm, "end": v(-76.9, 4.75) * mm});
            skLineSegment(sketch, "E414", {"start": v(-78.4, 2.55) * mm, "end": v(-77.7, 2.55) * mm});
            skLineSegment(sketch, "E415", {"start": v(-79.2, 4.75) * mm, "end": v(-78.4, 2.55) * mm});
            skLineSegment(sketch, "E416", {"start": v(-80.05, 4.75) * mm, "end": v(-79.2, 4.75) * mm});
            skLineSegment(sketch, "E417", {"start": v(-80.85, 2.55) * mm, "end": v(-80.05, 4.75) * mm});
            skLineSegment(sketch, "E418", {"start": v(-81.54, 2.55) * mm, "end": v(-80.85, 2.55) * mm});
            skLineSegment(sketch, "E419", {"start": v(-82.34, 4.75) * mm, "end": v(-81.54, 2.55) * mm});
            skLineSegment(sketch, "E420", {"start": v(-83.19, 4.75) * mm, "end": v(-82.34, 4.75) * mm});
            skLineSegment(sketch, "E421", {"start": v(-83.99, 2.55) * mm, "end": v(-83.19, 4.75) * mm});
            skLineSegment(sketch, "E422", {"start": v(-84.69, 2.55) * mm, "end": v(-83.99, 2.55) * mm});
            skLineSegment(sketch, "E423", {"start": v(-85.49, 4.75) * mm, "end": v(-84.69, 2.55) * mm});
            skLineSegment(sketch, "E424", {"start": v(-86.33, 4.75) * mm, "end": v(-85.49, 4.75) * mm});
            skLineSegment(sketch, "E425", {"start": v(-87.13, 2.55) * mm, "end": v(-86.33, 4.75) * mm});
            skLineSegment(sketch, "E426", {"start": v(-87.83, 2.55) * mm, "end": v(-87.13, 2.55) * mm});
            skLineSegment(sketch, "E427", {"start": v(-88.63, 4.75) * mm, "end": v(-87.83, 2.55) * mm});
            skLineSegment(sketch, "E428", {"start": v(-89.47, 4.75) * mm, "end": v(-88.63, 4.75) * mm});
            skLineSegment(sketch, "E429", {"start": v(-90.27, 2.55) * mm, "end": v(-89.47, 4.75) * mm});
            skLineSegment(sketch, "E430", {"start": v(-90.97, 2.55) * mm, "end": v(-90.27, 2.55) * mm});
            skLineSegment(sketch, "E431", {"start": v(-91.77, 4.75) * mm, "end": v(-90.97, 2.55) * mm});
            skLineSegment(sketch, "E432", {"start": v(-92.61, 4.75) * mm, "end": v(-91.77, 4.75) * mm});
            skLineSegment(sketch, "E433", {"start": v(-93.41, 2.55) * mm, "end": v(-92.61, 4.75) * mm});
            skLineSegment(sketch, "E434", {"start": v(-94.11, 2.55) * mm, "end": v(-93.41, 2.55) * mm});
            skLineSegment(sketch, "E435", {"start": v(-94.91, 4.75) * mm, "end": v(-94.11, 2.55) * mm});
            skLineSegment(sketch, "E436", {"start": v(-95.75, 4.75) * mm, "end": v(-94.91, 4.75) * mm});
            skLineSegment(sketch, "E437", {"start": v(-96.55, 2.55) * mm, "end": v(-95.75, 4.75) * mm});
            skLineSegment(sketch, "E438", {"start": v(-97.25, 2.55) * mm, "end": v(-96.55, 2.55) * mm});
            skLineSegment(sketch, "E439", {"start": v(-98.05, 4.75) * mm, "end": v(-97.25, 2.55) * mm});
            skLineSegment(sketch, "E440", {"start": v(-98.9, 4.75) * mm, "end": v(-98.05, 4.75) * mm});
            skLineSegment(sketch, "E441", {"start": v(-99.7, 2.55) * mm, "end": v(-98.9, 4.75) * mm});
            skLineSegment(sketch, "E442", {"start": v(-100.4, 2.55) * mm, "end": v(-99.7, 2.55) * mm});
            skLineSegment(sketch, "E443", {"start": v(-101.2, 4.75) * mm, "end": v(-100.4, 2.55) * mm});
            skLineSegment(sketch, "E444", {"start": v(-102.04, 4.75) * mm, "end": v(-101.2, 4.75) * mm});
            skLineSegment(sketch, "E445", {"start": v(-102.84, 2.55) * mm, "end": v(-102.04, 4.75) * mm});
            skLineSegment(sketch, "E446", {"start": v(-103.53, 2.55) * mm, "end": v(-102.84, 2.55) * mm});
            skLineSegment(sketch, "E447", {"start": v(-104.34, 4.75) * mm, "end": v(-103.53, 2.55) * mm});
            skLineSegment(sketch, "E448", {"start": v(-105.18, 4.75) * mm, "end": v(-104.34, 4.75) * mm});
            skLineSegment(sketch, "E449", {"start": v(-105.98, 2.55) * mm, "end": v(-105.18, 4.75) * mm});
            skLineSegment(sketch, "E450", {"start": v(-106.68, 2.55) * mm, "end": v(-105.98, 2.55) * mm});
            skLineSegment(sketch, "E451", {"start": v(-107.48, 4.75) * mm, "end": v(-106.68, 2.55) * mm});
            skLineSegment(sketch, "E452", {"start": v(-108.32, 4.75) * mm, "end": v(-107.48, 4.75) * mm});
            skLineSegment(sketch, "E453", {"start": v(-109.12, 2.55) * mm, "end": v(-108.32, 4.75) * mm});
            skLineSegment(sketch, "E454", {"start": v(-109.82, 2.55) * mm, "end": v(-109.12, 2.55) * mm});
            skLineSegment(sketch, "E455", {"start": v(-110.62, 4.75) * mm, "end": v(-109.82, 2.55) * mm});
            skLineSegment(sketch, "E456", {"start": v(-111.46, 4.75) * mm, "end": v(-110.62, 4.75) * mm});
            skLineSegment(sketch, "E457", {"start": v(-112.26, 2.55) * mm, "end": v(-111.46, 4.75) * mm});
            skLineSegment(sketch, "E458", {"start": v(-112.96, 2.55) * mm, "end": v(-112.26, 2.55) * mm});
            skLineSegment(sketch, "E459", {"start": v(-113.76, 4.75) * mm, "end": v(-112.96, 2.55) * mm});
            skLineSegment(sketch, "E460", {"start": v(-114.6, 4.75) * mm, "end": v(-113.76, 4.75) * mm});
            skLineSegment(sketch, "E461", {"start": v(-115.4, 2.55) * mm, "end": v(-114.6, 4.75) * mm});
            skLineSegment(sketch, "E462", {"start": v(-116.1, 2.55) * mm, "end": v(-115.4, 2.55) * mm});
            skLineSegment(sketch, "E463", {"start": v(-116.9, 4.75) * mm, "end": v(-116.1, 2.55) * mm});
            skLineSegment(sketch, "E464", {"start": v(-117.74, 4.75) * mm, "end": v(-116.9, 4.75) * mm});
            skLineSegment(sketch, "E465", {"start": v(-118.55, 2.55) * mm, "end": v(-117.74, 4.75) * mm});
            skLineSegment(sketch, "E466", {"start": v(-119.24, 2.55) * mm, "end": v(-118.55, 2.55) * mm});
            skLineSegment(sketch, "E467", {"start": v(-120.04, 4.75) * mm, "end": v(-119.24, 2.55) * mm});
            skLineSegment(sketch, "E468", {"start": v(-120.89, 4.75) * mm, "end": v(-120.04, 4.75) * mm});
            skLineSegment(sketch, "E469", {"start": v(-121.69, 2.55) * mm, "end": v(-120.89, 4.75) * mm});
            skLineSegment(sketch, "E470", {"start": v(-122.38, 2.55) * mm, "end": v(-121.69, 2.55) * mm});
            skLineSegment(sketch, "E471", {"start": v(-123.19, 4.75) * mm, "end": v(-122.38, 2.55) * mm});
            skLineSegment(sketch, "E472", {"start": v(-124.03, 4.75) * mm, "end": v(-123.19, 4.75) * mm});
            skLineSegment(sketch, "E473", {"start": v(-124.83, 2.55) * mm, "end": v(-124.03, 4.75) * mm});
            skLineSegment(sketch, "E474", {"start": v(-125.53, 2.55) * mm, "end": v(-124.83, 2.55) * mm});
            skLineSegment(sketch, "E475", {"start": v(-126.33, 4.75) * mm, "end": v(-125.53, 2.55) * mm});
            skLineSegment(sketch, "E476", {"start": v(-127.17, 4.75) * mm, "end": v(-126.33, 4.75) * mm});
            skLineSegment(sketch, "E477", {"start": v(-127.97, 2.55) * mm, "end": v(-127.17, 4.75) * mm});
            skLineSegment(sketch, "E478", {"start": v(-128.67, 2.55) * mm, "end": v(-127.97, 2.55) * mm});
            skLineSegment(sketch, "E479", {"start": v(-129.47, 4.75) * mm, "end": v(-128.67, 2.55) * mm});
            skLineSegment(sketch, "E480", {"start": v(-130.31, 4.75) * mm, "end": v(-129.47, 4.75) * mm});
            skLineSegment(sketch, "E481", {"start": v(-131.11, 2.55) * mm, "end": v(-130.31, 4.75) * mm});
            skLineSegment(sketch, "E482", {"start": v(-131.8, 2.55) * mm, "end": v(-131.11, 2.55) * mm});
            skLineSegment(sketch, "E483", {"start": v(-132.6, 4.75) * mm, "end": v(-131.8, 2.55) * mm});
            skLineSegment(sketch, "E484", {"start": v(-133.45, 4.75) * mm, "end": v(-132.6, 4.75) * mm});
            skLineSegment(sketch, "E485", {"start": v(-134.25, 2.55) * mm, "end": v(-133.45, 4.75) * mm});
            skLineSegment(sketch, "E486", {"start": v(-134.95, 2.55) * mm, "end": v(-134.25, 2.55) * mm});
            skLineSegment(sketch, "E487", {"start": v(-135.75, 4.75) * mm, "end": v(-134.95, 2.55) * mm});
            skLineSegment(sketch, "E488", {"start": v(-136.6, 4.75) * mm, "end": v(-135.75, 4.75) * mm});
            skLineSegment(sketch, "E489", {"start": v(-137.4, 2.55) * mm, "end": v(-136.6, 4.75) * mm});
            skLineSegment(sketch, "E490", {"start": v(-138.1, 2.55) * mm, "end": v(-137.4, 2.55) * mm});
            skLineSegment(sketch, "E491", {"start": v(-138.9, 4.75) * mm, "end": v(-138.1, 2.55) * mm});
            skLineSegment(sketch, "E492", {"start": v(-139.74, 4.75) * mm, "end": v(-138.9, 4.75) * mm});
            skLineSegment(sketch, "E493", {"start": v(-140.54, 2.55) * mm, "end": v(-139.74, 4.75) * mm});
            skLineSegment(sketch, "E494", {"start": v(-141.23, 2.55) * mm, "end": v(-140.54, 2.55) * mm});
            skLineSegment(sketch, "E495", {"start": v(-142.03, 4.75) * mm, "end": v(-141.23, 2.55) * mm});
            skLineSegment(sketch, "E496", {"start": v(-142.88, 4.75) * mm, "end": v(-142.03, 4.75) * mm});
            skLineSegment(sketch, "E497", {"start": v(-143.68, 2.55) * mm, "end": v(-142.88, 4.75) * mm});
            skLineSegment(sketch, "E498", {"start": v(-144.38, 2.55) * mm, "end": v(-143.68, 2.55) * mm});
            skLineSegment(sketch, "E499", {"start": v(-145.18, 4.75) * mm, "end": v(-144.38, 2.55) * mm});
            skLineSegment(sketch, "E500", {"start": v(-146.02, 4.75) * mm, "end": v(-145.18, 4.75) * mm});
            skLineSegment(sketch, "E501", {"start": v(-146.82, 2.55) * mm, "end": v(-146.02, 4.75) * mm});
            skLineSegment(sketch, "E502", {"start": v(-147.52, 2.55) * mm, "end": v(-146.82, 2.55) * mm});
            skLineSegment(sketch, "E503", {"start": v(-148.32, 4.75) * mm, "end": v(-147.52, 2.55) * mm});
            skLineSegment(sketch, "E504", {"start": v(-149.16, 4.75) * mm, "end": v(-148.32, 4.75) * mm});
            skLineSegment(sketch, "E505", {"start": v(-149.96, 2.55) * mm, "end": v(-149.16, 4.75) * mm});
            skLineSegment(sketch, "E506", {"start": v(-150.66, 2.55) * mm, "end": v(-149.96, 2.55) * mm});
            skLineSegment(sketch, "E507", {"start": v(-151.46, 4.75) * mm, "end": v(-150.66, 2.55) * mm});
            skLineSegment(sketch, "E508", {"start": v(-152.3, 4.75) * mm, "end": v(-151.46, 4.75) * mm});
            skLineSegment(sketch, "E509", {"start": v(-153.1, 2.55) * mm, "end": v(-152.3, 4.75) * mm});
            skLineSegment(sketch, "E510", {"start": v(-153.8, 2.55) * mm, "end": v(-153.1, 2.55) * mm});
            skLineSegment(sketch, "E511", {"start": v(-154.6, 4.75) * mm, "end": v(-153.8, 2.55) * mm});
            skLineSegment(sketch, "E512", {"start": v(-155.44, 4.75) * mm, "end": v(-154.6, 4.75) * mm});
            skLineSegment(sketch, "E513", {"start": v(-156.24, 2.55) * mm, "end": v(-155.44, 4.75) * mm});
            skLineSegment(sketch, "E514", {"start": v(-156.94, 2.55) * mm, "end": v(-156.24, 2.55) * mm});
            skLineSegment(sketch, "E515", {"start": v(-157.74, 4.75) * mm, "end": v(-156.94, 2.55) * mm});
            skLineSegment(sketch, "E516", {"start": v(-158.59, 4.75) * mm, "end": v(-157.74, 4.75) * mm});
            skLineSegment(sketch, "E517", {"start": v(-159.39, 2.55) * mm, "end": v(-158.59, 4.75) * mm});
            skLineSegment(sketch, "E518", {"start": v(-160.08, 2.55) * mm, "end": v(-159.39, 2.55) * mm});
            skLineSegment(sketch, "E519", {"start": v(-160.88, 4.75) * mm, "end": v(-160.08, 2.55) * mm});
            skLineSegment(sketch, "E520", {"start": v(-161.73, 4.75) * mm, "end": v(-160.88, 4.75) * mm});
            skLineSegment(sketch, "E521", {"start": v(-162.53, 2.55) * mm, "end": v(-161.73, 4.75) * mm});
            skLineSegment(sketch, "E522", {"start": v(-163.23, 2.55) * mm, "end": v(-162.53, 2.55) * mm});
            skLineSegment(sketch, "E523", {"start": v(-164.03, 4.75) * mm, "end": v(-163.23, 2.55) * mm});
            skLineSegment(sketch, "E524", {"start": v(-164.87, 4.75) * mm, "end": v(-164.03, 4.75) * mm});
            skLineSegment(sketch, "E525", {"start": v(-165.67, 2.55) * mm, "end": v(-164.87, 4.75) * mm});
            skLineSegment(sketch, "E526", {"start": v(-166.37, 2.55) * mm, "end": v(-165.67, 2.55) * mm});
            skLineSegment(sketch, "E527", {"start": v(-167.17, 4.75) * mm, "end": v(-166.37, 2.55) * mm});
            skLineSegment(sketch, "E528", {"start": v(-168.01, 4.75) * mm, "end": v(-167.17, 4.75) * mm});
            skLineSegment(sketch, "E529", {"start": v(-168.81, 2.55) * mm, "end": v(-168.01, 4.75) * mm});
            skLineSegment(sketch, "E530", {"start": v(-169.5, 2.55) * mm, "end": v(-168.81, 2.55) * mm});
            skLineSegment(sketch, "E531", {"start": v(-170.3, 4.75) * mm, "end": v(-169.5, 2.55) * mm});
            skLineSegment(sketch, "E532", {"start": v(-171.15, 4.75) * mm, "end": v(-170.3, 4.75) * mm});
            skLineSegment(sketch, "E533", {"start": v(-171.95, 2.55) * mm, "end": v(-171.15, 4.75) * mm});
            skLineSegment(sketch, "E534", {"start": v(-172.65, 2.55) * mm, "end": v(-171.95, 2.55) * mm});
            skLineSegment(sketch, "E535", {"start": v(-173.45, 4.75) * mm, "end": v(-172.65, 2.55) * mm});
            skLineSegment(sketch, "E536", {"start": v(-174.3, 4.75) * mm, "end": v(-173.45, 4.75) * mm});
            skLineSegment(sketch, "E537", {"start": v(-175.1, 2.55) * mm, "end": v(-174.3, 4.75) * mm});
            skLineSegment(sketch, "E538", {"start": v(-175.8, 2.55) * mm, "end": v(-175.1, 2.55) * mm});
            skLineSegment(sketch, "E539", {"start": v(-176.6, 4.75) * mm, "end": v(-175.8, 2.55) * mm});
            skLineSegment(sketch, "E540", {"start": v(-177.44, 4.75) * mm, "end": v(-176.6, 4.75) * mm});
            skLineSegment(sketch, "E541", {"start": v(-178.24, 2.55) * mm, "end": v(-177.44, 4.75) * mm});
            skLineSegment(sketch, "E542", {"start": v(-178.93, 2.55) * mm, "end": v(-178.24, 2.55) * mm});
            skLineSegment(sketch, "E543", {"start": v(-179.73, 4.75) * mm, "end": v(-178.93, 2.55) * mm});
            skLineSegment(sketch, "E544", {"start": v(-180.58, 4.75) * mm, "end": v(-179.73, 4.75) * mm});
            skLineSegment(sketch, "E545", {"start": v(-181.38, 2.55) * mm, "end": v(-180.58, 4.75) * mm});
            skLineSegment(sketch, "E546", {"start": v(-182.07, 2.55) * mm, "end": v(-181.38, 2.55) * mm});
            skLineSegment(sketch, "E547", {"start": v(-182.88, 4.75) * mm, "end": v(-182.07, 2.55) * mm});
            skLineSegment(sketch, "E548", {"start": v(-183.72, 4.75) * mm, "end": v(-182.88, 4.75) * mm});
            skLineSegment(sketch, "E549", {"start": v(-184.52, 2.55) * mm, "end": v(-183.72, 4.75) * mm});
            skLineSegment(sketch, "E550", {"start": v(-185.22, 2.55) * mm, "end": v(-184.52, 2.55) * mm});
            skLineSegment(sketch, "E551", {"start": v(-186.02, 4.75) * mm, "end": v(-185.22, 2.55) * mm});
            skLineSegment(sketch, "E552", {"start": v(-186.86, 4.75) * mm, "end": v(-186.02, 4.75) * mm});
            skLineSegment(sketch, "E553", {"start": v(-187.66, 2.55) * mm, "end": v(-186.86, 4.75) * mm});
            skLineSegment(sketch, "E554", {"start": v(-188.36, 2.55) * mm, "end": v(-187.66, 2.55) * mm});
            skLineSegment(sketch, "E555", {"start": v(-189.16, 4.75) * mm, "end": v(-188.36, 2.55) * mm});
            skLineSegment(sketch, "E556", {"start": v(-190, 4.75) * mm, "end": v(-189.16, 4.75) * mm});
            skLineSegment(sketch, "E557", {"start": v(-190.8, 2.55) * mm, "end": v(-190, 4.75) * mm});
            skLineSegment(sketch, "E558", {"start": v(-191.5, 2.55) * mm, "end": v(-190.8, 2.55) * mm});
            skLineSegment(sketch, "E559", {"start": v(-192.3, 4.75) * mm, "end": v(-191.5, 2.55) * mm});
            skLineSegment(sketch, "E560", {"start": v(-193.14, 4.75) * mm, "end": v(-192.3, 4.75) * mm});
            skLineSegment(sketch, "E561", {"start": v(-193.94, 2.55) * mm, "end": v(-193.14, 4.75) * mm});
            skLineSegment(sketch, "E562", {"start": v(-194.64, 2.55) * mm, "end": v(-193.94, 2.55) * mm});
            skLineSegment(sketch, "E563", {"start": v(-195.44, 4.75) * mm, "end": v(-194.64, 2.55) * mm});
            skLineSegment(sketch, "E564", {"start": v(-196.28, 4.75) * mm, "end": v(-195.44, 4.75) * mm});
            skLineSegment(sketch, "E565", {"start": v(-197.09, 2.55) * mm, "end": v(-196.28, 4.75) * mm});
            skLineSegment(sketch, "E566", {"start": v(-197.78, 2.55) * mm, "end": v(-197.09, 2.55) * mm});
            skLineSegment(sketch, "E567", {"start": v(-198.58, 4.75) * mm, "end": v(-197.78, 2.55) * mm});
            skLineSegment(sketch, "E568", {"start": v(-199.43, 4.75) * mm, "end": v(-198.58, 4.75) * mm});
            skLineSegment(sketch, "E569", {"start": v(-200.23, 2.55) * mm, "end": v(-199.43, 4.75) * mm});
            skLineSegment(sketch, "E570", {"start": v(-200.92, 2.55) * mm, "end": v(-200.23, 2.55) * mm});
            skLineSegment(sketch, "E571", {"start": v(-201.72, 4.75) * mm, "end": v(-200.92, 2.55) * mm});
            skLineSegment(sketch, "E572", {"start": v(-202.57, 4.75) * mm, "end": v(-201.72, 4.75) * mm});
            skLineSegment(sketch, "E573", {"start": v(-203.37, 2.55) * mm, "end": v(-202.57, 4.75) * mm});
            skLineSegment(sketch, "E574", {"start": v(-204.07, 2.55) * mm, "end": v(-203.37, 2.55) * mm});
            skLineSegment(sketch, "E575", {"start": v(-204.87, 4.75) * mm, "end": v(-204.07, 2.55) * mm});
            skLineSegment(sketch, "E576", {"start": v(-205.7, 4.75) * mm, "end": v(-204.87, 4.75) * mm});
            skLineSegment(sketch, "E577", {"start": v(-206.51, 2.55) * mm, "end": v(-205.7, 4.75) * mm});
            skLineSegment(sketch, "E578", {"start": v(-207.2, 2.55) * mm, "end": v(-206.51, 2.55) * mm});
            skLineSegment(sketch, "E579", {"start": v(-208, 4.75) * mm, "end": v(-207.2, 2.55) * mm});
            skLineSegment(sketch, "E580", {"start": v(-208.85, 4.75) * mm, "end": v(-208, 4.75) * mm});
            skLineSegment(sketch, "E581", {"start": v(-209.65, 2.55) * mm, "end": v(-208.85, 4.75) * mm});
            skLineSegment(sketch, "E582", {"start": v(-210.35, 2.55) * mm, "end": v(-209.65, 2.55) * mm});
            skLineSegment(sketch, "E583", {"start": v(-211.15, 4.75) * mm, "end": v(-210.35, 2.55) * mm});
            skLineSegment(sketch, "E584", {"start": v(-212, 4.75) * mm, "end": v(-211.15, 4.75) * mm});
            skLineSegment(sketch, "E585", {"start": v(-212.8, 2.55) * mm, "end": v(-212, 4.75) * mm});
            skLineSegment(sketch, "E586", {"start": v(-213.5, 2.55) * mm, "end": v(-212.8, 2.55) * mm});
            skLineSegment(sketch, "E587", {"start": v(-214.3, 4.75) * mm, "end": v(-213.5, 2.55) * mm});
            skLineSegment(sketch, "E588", {"start": v(-215.13, 4.75) * mm, "end": v(-214.3, 4.75) * mm});
            skLineSegment(sketch, "E589", {"start": v(-215.93, 2.55) * mm, "end": v(-215.13, 4.75) * mm});
            skLineSegment(sketch, "E590", {"start": v(-216.63, 2.55) * mm, "end": v(-215.93, 2.55) * mm});
            skLineSegment(sketch, "E591", {"start": v(-217.43, 4.75) * mm, "end": v(-216.63, 2.55) * mm});
            skLineSegment(sketch, "E592", {"start": v(-218.28, 4.75) * mm, "end": v(-217.43, 4.75) * mm});
            skLineSegment(sketch, "E593", {"start": v(-219.08, 2.55) * mm, "end": v(-218.28, 4.75) * mm});
            skLineSegment(sketch, "E594", {"start": v(-219.77, 2.55) * mm, "end": v(-219.08, 2.55) * mm});
            skLineSegment(sketch, "E595", {"start": v(-220.57, 4.75) * mm, "end": v(-219.77, 2.55) * mm});
            skLineSegment(sketch, "E596", {"start": v(-221.42, 4.75) * mm, "end": v(-220.57, 4.75) * mm});
            skLineSegment(sketch, "E597", {"start": v(-222.22, 2.55) * mm, "end": v(-221.42, 4.75) * mm});
            skLineSegment(sketch, "E598", {"start": v(-222.92, 2.55) * mm, "end": v(-222.22, 2.55) * mm});
            skLineSegment(sketch, "E599", {"start": v(-223.72, 4.75) * mm, "end": v(-222.92, 2.55) * mm});
            skLineSegment(sketch, "E600", {"start": v(-224.56, 4.75) * mm, "end": v(-223.72, 4.75) * mm});
            skLineSegment(sketch, "E601", {"start": v(-225.36, 2.55) * mm, "end": v(-224.56, 4.75) * mm});
            skLineSegment(sketch, "E602", {"start": v(-226.06, 2.55) * mm, "end": v(-225.36, 2.55) * mm});
            skLineSegment(sketch, "E603", {"start": v(-226.86, 4.75) * mm, "end": v(-226.06, 2.55) * mm});
            skLineSegment(sketch, "E604", {"start": v(-227.7, 4.75) * mm, "end": v(-226.86, 4.75) * mm});
            skLineSegment(sketch, "E605", {"start": v(-228.5, 2.55) * mm, "end": v(-227.7, 4.75) * mm});
            skLineSegment(sketch, "E606", {"start": v(-229.2, 2.55) * mm, "end": v(-228.5, 2.55) * mm});
            skLineSegment(sketch, "E607", {"start": v(-230, 4.75) * mm, "end": v(-229.2, 2.55) * mm});
            skLineSegment(sketch, "E608", {"start": v(-230.84, 4.75) * mm, "end": v(-230, 4.75) * mm});
            skLineSegment(sketch, "E609", {"start": v(-231.64, 2.55) * mm, "end": v(-230.84, 4.75) * mm});
            skLineSegment(sketch, "E610", {"start": v(-232.34, 2.55) * mm, "end": v(-231.64, 2.55) * mm});
            skLineSegment(sketch, "E611", {"start": v(-233.14, 4.75) * mm, "end": v(-232.34, 2.55) * mm});
            skLineSegment(sketch, "E612", {"start": v(-233.98, 4.75) * mm, "end": v(-233.14, 4.75) * mm});
            skLineSegment(sketch, "E613", {"start": v(-234.78, 2.55) * mm, "end": v(-233.98, 4.75) * mm});
            skLineSegment(sketch, "E614", {"start": v(-235.48, 2.55) * mm, "end": v(-234.78, 2.55) * mm});
            skLineSegment(sketch, "E615", {"start": v(-236.28, 4.75) * mm, "end": v(-235.48, 2.55) * mm});
            skLineSegment(sketch, "E616", {"start": v(-237.13, 4.75) * mm, "end": v(-236.28, 4.75) * mm});
            skLineSegment(sketch, "E617", {"start": v(-237.93, 2.55) * mm, "end": v(-237.13, 4.75) * mm});
            skLineSegment(sketch, "E618", {"start": v(-238.62, 2.55) * mm, "end": v(-237.93, 2.55) * mm});
            skLineSegment(sketch, "E619", {"start": v(-239.42, 4.75) * mm, "end": v(-238.62, 2.55) * mm});
            skLineSegment(sketch, "E620", {"start": v(-240.27, 4.75) * mm, "end": v(-239.42, 4.75) * mm});
            skLineSegment(sketch, "E621", {"start": v(-241.07, 2.55) * mm, "end": v(-240.27, 4.75) * mm});
            skLineSegment(sketch, "E622", {"start": v(-241.76, 2.55) * mm, "end": v(-241.07, 2.55) * mm});
            skLineSegment(sketch, "E623", {"start": v(-242.57, 4.75) * mm, "end": v(-241.76, 2.55) * mm});
            skLineSegment(sketch, "E624", {"start": v(-243.4, 4.75) * mm, "end": v(-242.57, 4.75) * mm});
            skLineSegment(sketch, "E625", {"start": v(-244.2, 2.55) * mm, "end": v(-243.4, 4.75) * mm});
            skLineSegment(sketch, "E626", {"start": v(-244.9, 2.55) * mm, "end": v(-244.2, 2.55) * mm});
            skLineSegment(sketch, "E627", {"start": v(-245.7, 4.75) * mm, "end": v(-244.9, 2.55) * mm});
            skLineSegment(sketch, "E628", {"start": v(-246.55, 4.75) * mm, "end": v(-245.7, 4.75) * mm});
            skLineSegment(sketch, "E629", {"start": v(-247.35, 2.55) * mm, "end": v(-246.55, 4.75) * mm});
            skLineSegment(sketch, "E630", {"start": v(-248.05, 2.55) * mm, "end": v(-247.35, 2.55) * mm});
            skLineSegment(sketch, "E631", {"start": v(-248.85, 4.75) * mm, "end": v(-248.05, 2.55) * mm});
            skLineSegment(sketch, "E632", {"start": v(-249.7, 4.75) * mm, "end": v(-248.85, 4.75) * mm});
            skLineSegment(sketch, "E633", {"start": v(-250.5, 2.55) * mm, "end": v(-249.7, 4.75) * mm});
            skLineSegment(sketch, "E634", {"start": v(-251.19, 2.55) * mm, "end": v(-250.5, 2.55) * mm});
            skLineSegment(sketch, "E635", {"start": v(-252, 4.75) * mm, "end": v(-251.19, 2.55) * mm});
            skLineSegment(sketch, "E636", {"start": v(-252.83, 4.75) * mm, "end": v(-252, 4.75) * mm});
            skLineSegment(sketch, "E637", {"start": v(-253.63, 2.55) * mm, "end": v(-252.83, 4.75) * mm});
            skLineSegment(sketch, "E638", {"start": v(-254.23, 2.55) * mm, "end": v(-253.63, 2.55) * mm});
            skLineSegment(sketch, "E639", {"start": v(-254.23, -5.25) * mm, "end": v(-254.23, 2.55) * mm});
            skLineSegment(sketch, "E640", {"start": v(44.72, 2.71) * mm, "end": v(44.72, -15.45) * mm});
            skLineSegment(sketch, "E641", {"start": v(57.3, -18.44) * mm, "end": v(-32.2, -18.44) * mm});
            skLineSegment(sketch, "E642", {"start": v(-50.4, 14.5) * mm, "end": v(-50.4, -18.88) * mm});
            skSolve(sketch);
        }
        {
            var Q0;
            Q0 = qSketchRegion(id + "F0", true);
            extrude(context, id + "F1", {"entities" : qUnion([Q0]), "depth" : 25 * mm});
        }
        {
            var Q0;
            Q0=makeQuery(id+"F1.opExtrude","CAP_FACE",FACE,{"disambiguationData":[OSD([sQuery(id+"F0.wireOp",EDGE,"E0"),sQuery(id+"F0.wireOp",EDGE,"E1"),sQuery(id+"F0.wireOp",EDGE,"E2"),sQuery(id+"F0.wireOp",EDGE,"E3"),sQuery(id+"F0.wireOp",EDGE,"E4"),sQuery(id+"F0.wireOp",EDGE,"E5"),sQuery(id+"F0.wireOp",EDGE,"E6"),sQuery(id+"F0.wireOp",EDGE,"E7"),sQuery(id+"F0.wireOp",EDGE,"E8"),sQuery(id+"F0.wireOp",EDGE,"E9"),sQuery(id+"F0.wireOp",EDGE,"E10"),sQuery(id+"F0.wireOp",EDGE,"E11"),sQuery(id+"F0.wireOp",EDGE,"E12"),sQuery(id+"F0.wireOp",EDGE,"E13"),sQuery(id+"F0.wireOp",EDGE,"E14"),sQuery(id+"F0.wireOp",EDGE,"E15"),sQuery(id+"F0.wireOp",EDGE,"E16"),sQuery(id+"F0.wireOp",EDGE,"E17"),sQuery(id+"F0.wireOp",EDGE,"E18"),sQuery(id+"F0.wireOp",EDGE,"E19"),sQuery(id+"F0.wireOp",EDGE,"E20"),sQuery(id+"F0.wireOp",EDGE,"E21"),sQuery(id+"F0.wireOp",EDGE,"E22"),sQuery(id+"F0.wireOp",EDGE,"E23"),sQuery(id+"F0.wireOp",EDGE,"E24"),sQuery(id+"F0.wireOp",EDGE,"E25"),sQuery(id+"F0.wireOp",EDGE,"E26"),sQuery(id+"F0.wireOp",EDGE,"E27"),sQuery(id+"F0.wireOp",EDGE,"E28"),sQuery(id+"F0.wireOp",EDGE,"E29"),sQuery(id+"F0.wireOp",EDGE,"E30"),sQuery(id+"F0.wireOp",EDGE,"E31"),sQuery(id+"F0.wireOp",EDGE,"E32"),sQuery(id+"F0.wireOp",EDGE,"E33"),sQuery(id+"F0.wireOp",EDGE,"E34"),sQuery(id+"F0.wireOp",EDGE,"E35"),sQuery(id+"F0.wireOp",EDGE,"E36"),sQuery(id+"F0.wireOp",EDGE,"E37"),sQuery(id+"F0.wireOp",EDGE,"E38"),sQuery(id+"F0.wireOp",EDGE,"E39"),sQuery(id+"F0.wireOp",EDGE,"E40"),sQuery(id+"F0.wireOp",EDGE,"E41"),sQuery(id+"F0.wireOp",EDGE,"E42"),sQuery(id+"F0.wireOp",EDGE,"E43"),sQuery(id+"F0.wireOp",EDGE,"E44"),sQuery(id+"F0.wireOp",EDGE,"E45"),sQuery(id+"F0.wireOp",EDGE,"E46"),sQuery(id+"F0.wireOp",EDGE,"E47"),sQuery(id+"F0.wireOp",EDGE,"E48"),sQuery(id+"F0.wireOp",EDGE,"E49"),sQuery(id+"F0.wireOp",EDGE,"E50"),sQuery(id+"F0.wireOp",EDGE,"E51"),sQuery(id+"F0.wireOp",EDGE,"E52"),sQuery(id+"F0.wireOp",EDGE,"E53"),sQuery(id+"F0.wireOp",EDGE,"E54"),sQuery(id+"F0.wireOp",EDGE,"E55"),sQuery(id+"F0.wireOp",EDGE,"E56"),sQuery(id+"F0.wireOp",EDGE,"E57"),sQuery(id+"F0.wireOp",EDGE,"E58"),sQuery(id+"F0.wireOp",EDGE,"E59"),sQuery(id+"F0.wireOp",EDGE,"E60"),sQuery(id+"F0.wireOp",EDGE,"E61"),sQuery(id+"F0.wireOp",EDGE,"E62"),sQuery(id+"F0.wireOp",EDGE,"E63"),sQuery(id+"F0.wireOp",EDGE,"E64"),sQuery(id+"F0.wireOp",EDGE,"E65"),sQuery(id+"F0.wireOp",EDGE,"E66"),sQuery(id+"F0.wireOp",EDGE,"E67"),sQuery(id+"F0.wireOp",EDGE,"E68"),sQuery(id+"F0.wireOp",EDGE,"E69"),sQuery(id+"F0.wireOp",EDGE,"E70"),sQuery(id+"F0.wireOp",EDGE,"E71"),sQuery(id+"F0.wireOp",EDGE,"E72"),sQuery(id+"F0.wireOp",EDGE,"E73"),sQuery(id+"F0.wireOp",EDGE,"E74"),sQuery(id+"F0.wireOp",EDGE,"E75"),sQuery(id+"F0.wireOp",EDGE,"E76"),sQuery(id+"F0.wireOp",EDGE,"E77"),sQuery(id+"F0.wireOp",EDGE,"E78"),sQuery(id+"F0.wireOp",EDGE,"E79"),sQuery(id+"F0.wireOp",EDGE,"E80"),sQuery(id+"F0.wireOp",EDGE,"E81"),sQuery(id+"F0.wireOp",EDGE,"E82"),sQuery(id+"F0.wireOp",EDGE,"E83"),sQuery(id+"F0.wireOp",EDGE,"E84"),sQuery(id+"F0.wireOp",EDGE,"E85"),sQuery(id+"F0.wireOp",EDGE,"E86"),sQuery(id+"F0.wireOp",EDGE,"E87"),sQuery(id+"F0.wireOp",EDGE,"E88"),sQuery(id+"F0.wireOp",EDGE,"E89"),sQuery(id+"F0.wireOp",EDGE,"E90"),sQuery(id+"F0.wireOp",EDGE,"E91"),sQuery(id+"F0.wireOp",EDGE,"E92"),sQuery(id+"F0.wireOp",EDGE,"E93"),sQuery(id+"F0.wireOp",EDGE,"E94"),sQuery(id+"F0.wireOp",EDGE,"E95"),sQuery(id+"F0.wireOp",EDGE,"E96"),sQuery(id+"F0.wireOp",EDGE,"E97"),sQuery(id+"F0.wireOp",EDGE,"E98"),sQuery(id+"F0.wireOp",EDGE,"E99"),sQuery(id+"F0.wireOp",EDGE,"E100"),sQuery(id+"F0.wireOp",EDGE,"E101"),sQuery(id+"F0.wireOp",EDGE,"E102"),sQuery(id+"F0.wireOp",EDGE,"E103"),sQuery(id+"F0.wireOp",EDGE,"E104"),sQuery(id+"F0.wireOp",EDGE,"E105"),sQuery(id+"F0.wireOp",EDGE,"E106"),sQuery(id+"F0.wireOp",EDGE,"E107"),sQuery(id+"F0.wireOp",EDGE,"E108"),sQuery(id+"F0.wireOp",EDGE,"E109"),sQuery(id+"F0.wireOp",EDGE,"E110"),sQuery(id+"F0.wireOp",EDGE,"E111"),sQuery(id+"F0.wireOp",EDGE,"E112"),sQuery(id+"F0.wireOp",EDGE,"E113"),sQuery(id+"F0.wireOp",EDGE,"E114"),sQuery(id+"F0.wireOp",EDGE,"E115"),sQuery(id+"F0.wireOp",EDGE,"E116"),sQuery(id+"F0.wireOp",EDGE,"E117"),sQuery(id+"F0.wireOp",EDGE,"E118"),sQuery(id+"F0.wireOp",EDGE,"E119"),sQuery(id+"F0.wireOp",EDGE,"E120"),sQuery(id+"F0.wireOp",EDGE,"E121"),sQuery(id+"F0.wireOp",EDGE,"E122"),sQuery(id+"F0.wireOp",EDGE,"E123"),sQuery(id+"F0.wireOp",EDGE,"E124"),sQuery(id+"F0.wireOp",EDGE,"E125"),sQuery(id+"F0.wireOp",EDGE,"E126"),sQuery(id+"F0.wireOp",EDGE,"E127"),sQuery(id+"F0.wireOp",EDGE,"E128"),sQuery(id+"F0.wireOp",EDGE,"E129"),sQuery(id+"F0.wireOp",EDGE,"E130"),sQuery(id+"F0.wireOp",EDGE,"E131"),sQuery(id+"F0.wireOp",EDGE,"E132"),sQuery(id+"F0.wireOp",EDGE,"E133"),sQuery(id+"F0.wireOp",EDGE,"E134"),sQuery(id+"F0.wireOp",EDGE,"E135"),sQuery(id+"F0.wireOp",EDGE,"E136"),sQuery(id+"F0.wireOp",EDGE,"E137"),sQuery(id+"F0.wireOp",EDGE,"E138"),sQuery(id+"F0.wireOp",EDGE,"E139"),sQuery(id+"F0.wireOp",EDGE,"E140"),sQuery(id+"F0.wireOp",EDGE,"E141"),sQuery(id+"F0.wireOp",EDGE,"E142"),sQuery(id+"F0.wireOp",EDGE,"E143"),sQuery(id+"F0.wireOp",EDGE,"E144"),sQuery(id+"F0.wireOp",EDGE,"E145"),sQuery(id+"F0.wireOp",EDGE,"E146"),sQuery(id+"F0.wireOp",EDGE,"E147"),sQuery(id+"F0.wireOp",EDGE,"E148"),sQuery(id+"F0.wireOp",EDGE,"E149"),sQuery(id+"F0.wireOp",EDGE,"E150"),sQuery(id+"F0.wireOp",EDGE,"E151"),sQuery(id+"F0.wireOp",EDGE,"E152"),sQuery(id+"F0.wireOp",EDGE,"E153"),sQuery(id+"F0.wireOp",EDGE,"E154"),sQuery(id+"F0.wireOp",EDGE,"E155"),sQuery(id+"F0.wireOp",EDGE,"E156"),sQuery(id+"F0.wireOp",EDGE,"E157"),sQuery(id+"F0.wireOp",EDGE,"E158"),sQuery(id+"F0.wireOp",EDGE,"E159"),sQuery(id+"F0.wireOp",EDGE,"E160"),sQuery(id+"F0.wireOp",EDGE,"E161"),sQuery(id+"F0.wireOp",EDGE,"E162"),sQuery(id+"F0.wireOp",EDGE,"E163"),sQuery(id+"F0.wireOp",EDGE,"E164"),sQuery(id+"F0.wireOp",EDGE,"E165"),sQuery(id+"F0.wireOp",EDGE,"E166"),sQuery(id+"F0.wireOp",EDGE,"E167"),sQuery(id+"F0.wireOp",EDGE,"E168"),sQuery(id+"F0.wireOp",EDGE,"E169"),sQuery(id+"F0.wireOp",EDGE,"E170"),sQuery(id+"F0.wireOp",EDGE,"E171"),sQuery(id+"F0.wireOp",EDGE,"E172"),sQuery(id+"F0.wireOp",EDGE,"E173"),sQuery(id+"F0.wireOp",EDGE,"E174"),sQuery(id+"F0.wireOp",EDGE,"E175"),sQuery(id+"F0.wireOp",EDGE,"E176"),sQuery(id+"F0.wireOp",EDGE,"E177"),sQuery(id+"F0.wireOp",EDGE,"E178"),sQuery(id+"F0.wireOp",EDGE,"E179"),sQuery(id+"F0.wireOp",EDGE,"E180"),sQuery(id+"F0.wireOp",EDGE,"E181"),sQuery(id+"F0.wireOp",EDGE,"E182"),sQuery(id+"F0.wireOp",EDGE,"E183"),sQuery(id+"F0.wireOp",EDGE,"E184"),sQuery(id+"F0.wireOp",EDGE,"E185"),sQuery(id+"F0.wireOp",EDGE,"E186"),sQuery(id+"F0.wireOp",EDGE,"E187"),sQuery(id+"F0.wireOp",EDGE,"E188"),sQuery(id+"F0.wireOp",EDGE,"E189"),sQuery(id+"F0.wireOp",EDGE,"E190"),sQuery(id+"F0.wireOp",EDGE,"E191"),sQuery(id+"F0.wireOp",EDGE,"E192"),sQuery(id+"F0.wireOp",EDGE,"E193"),sQuery(id+"F0.wireOp",EDGE,"E194"),sQuery(id+"F0.wireOp",EDGE,"E195"),sQuery(id+"F0.wireOp",EDGE,"E196"),sQuery(id+"F0.wireOp",EDGE,"E197"),sQuery(id+"F0.wireOp",EDGE,"E198"),sQuery(id+"F0.wireOp",EDGE,"E199"),sQuery(id+"F0.wireOp",EDGE,"E200"),sQuery(id+"F0.wireOp",EDGE,"E201"),sQuery(id+"F0.wireOp",EDGE,"E202"),sQuery(id+"F0.wireOp",EDGE,"E203"),sQuery(id+"F0.wireOp",EDGE,"E204"),sQuery(id+"F0.wireOp",EDGE,"E205"),sQuery(id+"F0.wireOp",EDGE,"E206"),sQuery(id+"F0.wireOp",EDGE,"E207"),sQuery(id+"F0.wireOp",EDGE,"E208"),sQuery(id+"F0.wireOp",EDGE,"E209"),sQuery(id+"F0.wireOp",EDGE,"E210"),sQuery(id+"F0.wireOp",EDGE,"E211"),sQuery(id+"F0.wireOp",EDGE,"E212"),sQuery(id+"F0.wireOp",EDGE,"E213"),sQuery(id+"F0.wireOp",EDGE,"E214"),sQuery(id+"F0.wireOp",EDGE,"E215"),sQuery(id+"F0.wireOp",EDGE,"E216"),sQuery(id+"F0.wireOp",EDGE,"E217"),sQuery(id+"F0.wireOp",EDGE,"E218"),sQuery(id+"F0.wireOp",EDGE,"E219"),sQuery(id+"F0.wireOp",EDGE,"E220"),sQuery(id+"F0.wireOp",EDGE,"E221"),sQuery(id+"F0.wireOp",EDGE,"E222"),sQuery(id+"F0.wireOp",EDGE,"E223"),sQuery(id+"F0.wireOp",EDGE,"E224"),sQuery(id+"F0.wireOp",EDGE,"E225"),sQuery(id+"F0.wireOp",EDGE,"E226"),sQuery(id+"F0.wireOp",EDGE,"E227"),sQuery(id+"F0.wireOp",EDGE,"E228"),sQuery(id+"F0.wireOp",EDGE,"E229"),sQuery(id+"F0.wireOp",EDGE,"E230"),sQuery(id+"F0.wireOp",EDGE,"E231"),sQuery(id+"F0.wireOp",EDGE,"E232"),sQuery(id+"F0.wireOp",EDGE,"E233"),sQuery(id+"F0.wireOp",EDGE,"E234"),sQuery(id+"F0.wireOp",EDGE,"E235"),sQuery(id+"F0.wireOp",EDGE,"E236"),sQuery(id+"F0.wireOp",EDGE,"E237"),sQuery(id+"F0.wireOp",EDGE,"E238"),sQuery(id+"F0.wireOp",EDGE,"E239"),sQuery(id+"F0.wireOp",EDGE,"E240"),sQuery(id+"F0.wireOp",EDGE,"E241"),sQuery(id+"F0.wireOp",EDGE,"E242"),sQuery(id+"F0.wireOp",EDGE,"E243"),sQuery(id+"F0.wireOp",EDGE,"E244"),sQuery(id+"F0.wireOp",EDGE,"E245"),sQuery(id+"F0.wireOp",EDGE,"E246"),sQuery(id+"F0.wireOp",EDGE,"E247"),sQuery(id+"F0.wireOp",EDGE,"E248"),sQuery(id+"F0.wireOp",EDGE,"E249"),sQuery(id+"F0.wireOp",EDGE,"E250"),sQuery(id+"F0.wireOp",EDGE,"E251"),sQuery(id+"F0.wireOp",EDGE,"E252"),sQuery(id+"F0.wireOp",EDGE,"E253"),sQuery(id+"F0.wireOp",EDGE,"E254"),sQuery(id+"F0.wireOp",EDGE,"E255"),sQuery(id+"F0.wireOp",EDGE,"E256"),sQuery(id+"F0.wireOp",EDGE,"E257"),sQuery(id+"F0.wireOp",EDGE,"E258"),sQuery(id+"F0.wireOp",EDGE,"E259"),sQuery(id+"F0.wireOp",EDGE,"E260"),sQuery(id+"F0.wireOp",EDGE,"E261"),sQuery(id+"F0.wireOp",EDGE,"E262"),sQuery(id+"F0.wireOp",EDGE,"E263"),sQuery(id+"F0.wireOp",EDGE,"E264"),sQuery(id+"F0.wireOp",EDGE,"E265"),sQuery(id+"F0.wireOp",EDGE,"E266"),sQuery(id+"F0.wireOp",EDGE,"E267"),sQuery(id+"F0.wireOp",EDGE,"E268"),sQuery(id+"F0.wireOp",EDGE,"E269"),sQuery(id+"F0.wireOp",EDGE,"E270"),sQuery(id+"F0.wireOp",EDGE,"E271"),sQuery(id+"F0.wireOp",EDGE,"E272"),sQuery(id+"F0.wireOp",EDGE,"E273"),sQuery(id+"F0.wireOp",EDGE,"E274"),sQuery(id+"F0.wireOp",EDGE,"E275"),sQuery(id+"F0.wireOp",EDGE,"E276"),sQuery(id+"F0.wireOp",EDGE,"E277"),sQuery(id+"F0.wireOp",EDGE,"E278"),sQuery(id+"F0.wireOp",EDGE,"E279"),sQuery(id+"F0.wireOp",EDGE,"E280"),sQuery(id+"F0.wireOp",EDGE,"E281"),sQuery(id+"F0.wireOp",EDGE,"E282"),sQuery(id+"F0.wireOp",EDGE,"E283"),sQuery(id+"F0.wireOp",EDGE,"E284"),sQuery(id+"F0.wireOp",EDGE,"E285"),sQuery(id+"F0.wireOp",EDGE,"E286"),sQuery(id+"F0.wireOp",EDGE,"E287"),sQuery(id+"F0.wireOp",EDGE,"E288"),sQuery(id+"F0.wireOp",EDGE,"E289"),sQuery(id+"F0.wireOp",EDGE,"E290"),sQuery(id+"F0.wireOp",EDGE,"E291"),sQuery(id+"F0.wireOp",EDGE,"E292"),sQuery(id+"F0.wireOp",EDGE,"E293"),sQuery(id+"F0.wireOp",EDGE,"E294"),sQuery(id+"F0.wireOp",EDGE,"E295"),sQuery(id+"F0.wireOp",EDGE,"E296"),sQuery(id+"F0.wireOp",EDGE,"E297"),sQuery(id+"F0.wireOp",EDGE,"E298"),sQuery(id+"F0.wireOp",EDGE,"E299"),sQuery(id+"F0.wireOp",EDGE,"E300"),sQuery(id+"F0.wireOp",EDGE,"E301"),sQuery(id+"F0.wireOp",EDGE,"E302"),sQuery(id+"F0.wireOp",EDGE,"E303"),sQuery(id+"F0.wireOp",EDGE,"E304"),sQuery(id+"F0.wireOp",EDGE,"E305"),sQuery(id+"F0.wireOp",EDGE,"E306"),sQuery(id+"F0.wireOp",EDGE,"E307"),sQuery(id+"F0.wireOp",EDGE,"E308"),sQuery(id+"F0.wireOp",EDGE,"E309"),sQuery(id+"F0.wireOp",EDGE,"E310"),sQuery(id+"F0.wireOp",EDGE,"E311"),sQuery(id+"F0.wireOp",EDGE,"E312"),sQuery(id+"F0.wireOp",EDGE,"E313"),sQuery(id+"F0.wireOp",EDGE,"E314"),sQuery(id+"F0.wireOp",EDGE,"E315"),sQuery(id+"F0.wireOp",EDGE,"E316"),sQuery(id+"F0.wireOp",EDGE,"E317"),sQuery(id+"F0.wireOp",EDGE,"E318"),sQuery(id+"F0.wireOp",EDGE,"E319"),sQuery(id+"F0.wireOp",EDGE,"E320"),sQuery(id+"F0.wireOp",EDGE,"E321"),sQuery(id+"F0.wireOp",EDGE,"E322"),sQuery(id+"F0.wireOp",EDGE,"E323"),sQuery(id+"F0.wireOp",EDGE,"E324"),sQuery(id+"F0.wireOp",EDGE,"E325"),sQuery(id+"F0.wireOp",EDGE,"E326"),sQuery(id+"F0.wireOp",EDGE,"E327"),sQuery(id+"F0.wireOp",EDGE,"E328"),sQuery(id+"F0.wireOp",EDGE,"E329"),sQuery(id+"F0.wireOp",EDGE,"E330"),sQuery(id+"F0.wireOp",EDGE,"E331"),sQuery(id+"F0.wireOp",EDGE,"E332"),sQuery(id+"F0.wireOp",EDGE,"E333"),sQuery(id+"F0.wireOp",EDGE,"E334"),sQuery(id+"F0.wireOp",EDGE,"E335"),sQuery(id+"F0.wireOp",EDGE,"E336"),sQuery(id+"F0.wireOp",EDGE,"E337"),sQuery(id+"F0.wireOp",EDGE,"E338"),sQuery(id+"F0.wireOp",EDGE,"E339"),sQuery(id+"F0.wireOp",EDGE,"E340"),sQuery(id+"F0.wireOp",EDGE,"E341"),sQuery(id+"F0.wireOp",EDGE,"E342"),sQuery(id+"F0.wireOp",EDGE,"E343"),sQuery(id+"F0.wireOp",EDGE,"E344"),sQuery(id+"F0.wireOp",EDGE,"E345"),sQuery(id+"F0.wireOp",EDGE,"E346"),sQuery(id+"F0.wireOp",EDGE,"E347"),sQuery(id+"F0.wireOp",EDGE,"E348"),sQuery(id+"F0.wireOp",EDGE,"E349"),sQuery(id+"F0.wireOp",EDGE,"E350"),sQuery(id+"F0.wireOp",EDGE,"E351"),sQuery(id+"F0.wireOp",EDGE,"E352"),sQuery(id+"F0.wireOp",EDGE,"E353"),sQuery(id+"F0.wireOp",EDGE,"E354"),sQuery(id+"F0.wireOp",EDGE,"E355"),sQuery(id+"F0.wireOp",EDGE,"E356"),sQuery(id+"F0.wireOp",EDGE,"E357"),sQuery(id+"F0.wireOp",EDGE,"E358"),sQuery(id+"F0.wireOp",EDGE,"E359"),sQuery(id+"F0.wireOp",EDGE,"E360"),sQuery(id+"F0.wireOp",EDGE,"E361"),sQuery(id+"F0.wireOp",EDGE,"E362"),sQuery(id+"F0.wireOp",EDGE,"E363"),sQuery(id+"F0.wireOp",EDGE,"E364"),sQuery(id+"F0.wireOp",EDGE,"E365"),sQuery(id+"F0.wireOp",EDGE,"E366"),sQuery(id+"F0.wireOp",EDGE,"E367"),sQuery(id+"F0.wireOp",EDGE,"E368"),sQuery(id+"F0.wireOp",EDGE,"E369"),sQuery(id+"F0.wireOp",EDGE,"E370"),sQuery(id+"F0.wireOp",EDGE,"E371"),sQuery(id+"F0.wireOp",EDGE,"E372"),sQuery(id+"F0.wireOp",EDGE,"E373"),sQuery(id+"F0.wireOp",EDGE,"E374"),sQuery(id+"F0.wireOp",EDGE,"E375"),sQuery(id+"F0.wireOp",EDGE,"E376"),sQuery(id+"F0.wireOp",EDGE,"E377"),sQuery(id+"F0.wireOp",EDGE,"E378"),sQuery(id+"F0.wireOp",EDGE,"E379"),sQuery(id+"F0.wireOp",EDGE,"E642")])],"isStart":false});
            var sketch = newSketch(context, id + "F2", { "sketchPlane" : qUnion([Q0])});
            skLineSegment(sketch, "E643", {"start": v(110.8, 2.55) * mm, "end": v(110.8, -7.74) * mm});
            skSolve(sketch);
        }
        {
            var Q0;
            Q0 = qSketchRegion(id + "F2", true);
            var Q1;
            Q1=makeQuery(id+"F2.imprint","IMPRINT",FACE,{"disambiguationData":[TD([[makeQuery(id+"F2.imprint","IMPRINT",EDGE,{"derivedFrom":makeQuery(id+"F1.opExtrude","CAP_EDGE",EDGE,{"disambiguationData":[OSD([sQuery(id+"F0.wireOp",EDGE,"E0")])],"isStart":false})}),-1.0]])]});
            extrude(context, id + "F3", {"entities" : qUnion([Q0, Q1]), "operationType" : NewBodyOperationType.REMOVE, "oppositeDirection" : true, "depth" : 26 * mm});
        }
        {
            var Q0;
            Q0=makeQuery(id+"F1.opExtrude","CAP_FACE",FACE,{"disambiguationData":[OSD([sQuery(id+"F0.wireOp",EDGE,"E0"),sQuery(id+"F0.wireOp",EDGE,"E1"),sQuery(id+"F0.wireOp",EDGE,"E2"),sQuery(id+"F0.wireOp",EDGE,"E3"),sQuery(id+"F0.wireOp",EDGE,"E4"),sQuery(id+"F0.wireOp",EDGE,"E5"),sQuery(id+"F0.wireOp",EDGE,"E6"),sQuery(id+"F0.wireOp",EDGE,"E7"),sQuery(id+"F0.wireOp",EDGE,"E8"),sQuery(id+"F0.wireOp",EDGE,"E9"),sQuery(id+"F0.wireOp",EDGE,"E10"),sQuery(id+"F0.wireOp",EDGE,"E11"),sQuery(id+"F0.wireOp",EDGE,"E12"),sQuery(id+"F0.wireOp",EDGE,"E13"),sQuery(id+"F0.wireOp",EDGE,"E14"),sQuery(id+"F0.wireOp",EDGE,"E15"),sQuery(id+"F0.wireOp",EDGE,"E16"),sQuery(id+"F0.wireOp",EDGE,"E17"),sQuery(id+"F0.wireOp",EDGE,"E18"),sQuery(id+"F0.wireOp",EDGE,"E19"),sQuery(id+"F0.wireOp",EDGE,"E20"),sQuery(id+"F0.wireOp",EDGE,"E21"),sQuery(id+"F0.wireOp",EDGE,"E22"),sQuery(id+"F0.wireOp",EDGE,"E23"),sQuery(id+"F0.wireOp",EDGE,"E24"),sQuery(id+"F0.wireOp",EDGE,"E25"),sQuery(id+"F0.wireOp",EDGE,"E26"),sQuery(id+"F0.wireOp",EDGE,"E27"),sQuery(id+"F0.wireOp",EDGE,"E28"),sQuery(id+"F0.wireOp",EDGE,"E29"),sQuery(id+"F0.wireOp",EDGE,"E30"),sQuery(id+"F0.wireOp",EDGE,"E31"),sQuery(id+"F0.wireOp",EDGE,"E32"),sQuery(id+"F0.wireOp",EDGE,"E33"),sQuery(id+"F0.wireOp",EDGE,"E34"),sQuery(id+"F0.wireOp",EDGE,"E35"),sQuery(id+"F0.wireOp",EDGE,"E36"),sQuery(id+"F0.wireOp",EDGE,"E37"),sQuery(id+"F0.wireOp",EDGE,"E38"),sQuery(id+"F0.wireOp",EDGE,"E39"),sQuery(id+"F0.wireOp",EDGE,"E40"),sQuery(id+"F0.wireOp",EDGE,"E41"),sQuery(id+"F0.wireOp",EDGE,"E42"),sQuery(id+"F0.wireOp",EDGE,"E43"),sQuery(id+"F0.wireOp",EDGE,"E44"),sQuery(id+"F0.wireOp",EDGE,"E45"),sQuery(id+"F0.wireOp",EDGE,"E46"),sQuery(id+"F0.wireOp",EDGE,"E47"),sQuery(id+"F0.wireOp",EDGE,"E48"),sQuery(id+"F0.wireOp",EDGE,"E49"),sQuery(id+"F0.wireOp",EDGE,"E50"),sQuery(id+"F0.wireOp",EDGE,"E51"),sQuery(id+"F0.wireOp",EDGE,"E52"),sQuery(id+"F0.wireOp",EDGE,"E53"),sQuery(id+"F0.wireOp",EDGE,"E54"),sQuery(id+"F0.wireOp",EDGE,"E55"),sQuery(id+"F0.wireOp",EDGE,"E56"),sQuery(id+"F0.wireOp",EDGE,"E57"),sQuery(id+"F0.wireOp",EDGE,"E58"),sQuery(id+"F0.wireOp",EDGE,"E59"),sQuery(id+"F0.wireOp",EDGE,"E60"),sQuery(id+"F0.wireOp",EDGE,"E61"),sQuery(id+"F0.wireOp",EDGE,"E62"),sQuery(id+"F0.wireOp",EDGE,"E63"),sQuery(id+"F0.wireOp",EDGE,"E64"),sQuery(id+"F0.wireOp",EDGE,"E65"),sQuery(id+"F0.wireOp",EDGE,"E66"),sQuery(id+"F0.wireOp",EDGE,"E67"),sQuery(id+"F0.wireOp",EDGE,"E68"),sQuery(id+"F0.wireOp",EDGE,"E69"),sQuery(id+"F0.wireOp",EDGE,"E70"),sQuery(id+"F0.wireOp",EDGE,"E71"),sQuery(id+"F0.wireOp",EDGE,"E72"),sQuery(id+"F0.wireOp",EDGE,"E73"),sQuery(id+"F0.wireOp",EDGE,"E74"),sQuery(id+"F0.wireOp",EDGE,"E75"),sQuery(id+"F0.wireOp",EDGE,"E76"),sQuery(id+"F0.wireOp",EDGE,"E77"),sQuery(id+"F0.wireOp",EDGE,"E78"),sQuery(id+"F0.wireOp",EDGE,"E79"),sQuery(id+"F0.wireOp",EDGE,"E80"),sQuery(id+"F0.wireOp",EDGE,"E81"),sQuery(id+"F0.wireOp",EDGE,"E82"),sQuery(id+"F0.wireOp",EDGE,"E83"),sQuery(id+"F0.wireOp",EDGE,"E84"),sQuery(id+"F0.wireOp",EDGE,"E85"),sQuery(id+"F0.wireOp",EDGE,"E86"),sQuery(id+"F0.wireOp",EDGE,"E87"),sQuery(id+"F0.wireOp",EDGE,"E88"),sQuery(id+"F0.wireOp",EDGE,"E89"),sQuery(id+"F0.wireOp",EDGE,"E90"),sQuery(id+"F0.wireOp",EDGE,"E91"),sQuery(id+"F0.wireOp",EDGE,"E92"),sQuery(id+"F0.wireOp",EDGE,"E93"),sQuery(id+"F0.wireOp",EDGE,"E94"),sQuery(id+"F0.wireOp",EDGE,"E95"),sQuery(id+"F0.wireOp",EDGE,"E96"),sQuery(id+"F0.wireOp",EDGE,"E97"),sQuery(id+"F0.wireOp",EDGE,"E98"),sQuery(id+"F0.wireOp",EDGE,"E99"),sQuery(id+"F0.wireOp",EDGE,"E100"),sQuery(id+"F0.wireOp",EDGE,"E101"),sQuery(id+"F0.wireOp",EDGE,"E102"),sQuery(id+"F0.wireOp",EDGE,"E103"),sQuery(id+"F0.wireOp",EDGE,"E104"),sQuery(id+"F0.wireOp",EDGE,"E105"),sQuery(id+"F0.wireOp",EDGE,"E106"),sQuery(id+"F0.wireOp",EDGE,"E107"),sQuery(id+"F0.wireOp",EDGE,"E108"),sQuery(id+"F0.wireOp",EDGE,"E109"),sQuery(id+"F0.wireOp",EDGE,"E110"),sQuery(id+"F0.wireOp",EDGE,"E111"),sQuery(id+"F0.wireOp",EDGE,"E112"),sQuery(id+"F0.wireOp",EDGE,"E113"),sQuery(id+"F0.wireOp",EDGE,"E114"),sQuery(id+"F0.wireOp",EDGE,"E115"),sQuery(id+"F0.wireOp",EDGE,"E116"),sQuery(id+"F0.wireOp",EDGE,"E117"),sQuery(id+"F0.wireOp",EDGE,"E118"),sQuery(id+"F0.wireOp",EDGE,"E119"),sQuery(id+"F0.wireOp",EDGE,"E120"),sQuery(id+"F0.wireOp",EDGE,"E121"),sQuery(id+"F0.wireOp",EDGE,"E122"),sQuery(id+"F0.wireOp",EDGE,"E123"),sQuery(id+"F0.wireOp",EDGE,"E124"),sQuery(id+"F0.wireOp",EDGE,"E125"),sQuery(id+"F0.wireOp",EDGE,"E126"),sQuery(id+"F0.wireOp",EDGE,"E127"),sQuery(id+"F0.wireOp",EDGE,"E128"),sQuery(id+"F0.wireOp",EDGE,"E129"),sQuery(id+"F0.wireOp",EDGE,"E130"),sQuery(id+"F0.wireOp",EDGE,"E131"),sQuery(id+"F0.wireOp",EDGE,"E132"),sQuery(id+"F0.wireOp",EDGE,"E133"),sQuery(id+"F0.wireOp",EDGE,"E134"),sQuery(id+"F0.wireOp",EDGE,"E135"),sQuery(id+"F0.wireOp",EDGE,"E136"),sQuery(id+"F0.wireOp",EDGE,"E137"),sQuery(id+"F0.wireOp",EDGE,"E138"),sQuery(id+"F0.wireOp",EDGE,"E139"),sQuery(id+"F0.wireOp",EDGE,"E140"),sQuery(id+"F0.wireOp",EDGE,"E141"),sQuery(id+"F0.wireOp",EDGE,"E142"),sQuery(id+"F0.wireOp",EDGE,"E143"),sQuery(id+"F0.wireOp",EDGE,"E144"),sQuery(id+"F0.wireOp",EDGE,"E145"),sQuery(id+"F0.wireOp",EDGE,"E146"),sQuery(id+"F0.wireOp",EDGE,"E147"),sQuery(id+"F0.wireOp",EDGE,"E148"),sQuery(id+"F0.wireOp",EDGE,"E149"),sQuery(id+"F0.wireOp",EDGE,"E150"),sQuery(id+"F0.wireOp",EDGE,"E151"),sQuery(id+"F0.wireOp",EDGE,"E152"),sQuery(id+"F0.wireOp",EDGE,"E153"),sQuery(id+"F0.wireOp",EDGE,"E154"),sQuery(id+"F0.wireOp",EDGE,"E155"),sQuery(id+"F0.wireOp",EDGE,"E156"),sQuery(id+"F0.wireOp",EDGE,"E157"),sQuery(id+"F0.wireOp",EDGE,"E158"),sQuery(id+"F0.wireOp",EDGE,"E159"),sQuery(id+"F0.wireOp",EDGE,"E160"),sQuery(id+"F0.wireOp",EDGE,"E161"),sQuery(id+"F0.wireOp",EDGE,"E162"),sQuery(id+"F0.wireOp",EDGE,"E163"),sQuery(id+"F0.wireOp",EDGE,"E164"),sQuery(id+"F0.wireOp",EDGE,"E165"),sQuery(id+"F0.wireOp",EDGE,"E166"),sQuery(id+"F0.wireOp",EDGE,"E167"),sQuery(id+"F0.wireOp",EDGE,"E168"),sQuery(id+"F0.wireOp",EDGE,"E169"),sQuery(id+"F0.wireOp",EDGE,"E170"),sQuery(id+"F0.wireOp",EDGE,"E171"),sQuery(id+"F0.wireOp",EDGE,"E172"),sQuery(id+"F0.wireOp",EDGE,"E173"),sQuery(id+"F0.wireOp",EDGE,"E174"),sQuery(id+"F0.wireOp",EDGE,"E175"),sQuery(id+"F0.wireOp",EDGE,"E176"),sQuery(id+"F0.wireOp",EDGE,"E177"),sQuery(id+"F0.wireOp",EDGE,"E178"),sQuery(id+"F0.wireOp",EDGE,"E179"),sQuery(id+"F0.wireOp",EDGE,"E180"),sQuery(id+"F0.wireOp",EDGE,"E181"),sQuery(id+"F0.wireOp",EDGE,"E182"),sQuery(id+"F0.wireOp",EDGE,"E183"),sQuery(id+"F0.wireOp",EDGE,"E184"),sQuery(id+"F0.wireOp",EDGE,"E185"),sQuery(id+"F0.wireOp",EDGE,"E186"),sQuery(id+"F0.wireOp",EDGE,"E187"),sQuery(id+"F0.wireOp",EDGE,"E188"),sQuery(id+"F0.wireOp",EDGE,"E189"),sQuery(id+"F0.wireOp",EDGE,"E190"),sQuery(id+"F0.wireOp",EDGE,"E191"),sQuery(id+"F0.wireOp",EDGE,"E192"),sQuery(id+"F0.wireOp",EDGE,"E193"),sQuery(id+"F0.wireOp",EDGE,"E194"),sQuery(id+"F0.wireOp",EDGE,"E195"),sQuery(id+"F0.wireOp",EDGE,"E196"),sQuery(id+"F0.wireOp",EDGE,"E197"),sQuery(id+"F0.wireOp",EDGE,"E198"),sQuery(id+"F0.wireOp",EDGE,"E199"),sQuery(id+"F0.wireOp",EDGE,"E200"),sQuery(id+"F0.wireOp",EDGE,"E201"),sQuery(id+"F0.wireOp",EDGE,"E202"),sQuery(id+"F0.wireOp",EDGE,"E203"),sQuery(id+"F0.wireOp",EDGE,"E204"),sQuery(id+"F0.wireOp",EDGE,"E205"),sQuery(id+"F0.wireOp",EDGE,"E206"),sQuery(id+"F0.wireOp",EDGE,"E207"),sQuery(id+"F0.wireOp",EDGE,"E208"),sQuery(id+"F0.wireOp",EDGE,"E209"),sQuery(id+"F0.wireOp",EDGE,"E210"),sQuery(id+"F0.wireOp",EDGE,"E211"),sQuery(id+"F0.wireOp",EDGE,"E212"),sQuery(id+"F0.wireOp",EDGE,"E213"),sQuery(id+"F0.wireOp",EDGE,"E214"),sQuery(id+"F0.wireOp",EDGE,"E215"),sQuery(id+"F0.wireOp",EDGE,"E216"),sQuery(id+"F0.wireOp",EDGE,"E217"),sQuery(id+"F0.wireOp",EDGE,"E218"),sQuery(id+"F0.wireOp",EDGE,"E219"),sQuery(id+"F0.wireOp",EDGE,"E220"),sQuery(id+"F0.wireOp",EDGE,"E221"),sQuery(id+"F0.wireOp",EDGE,"E222"),sQuery(id+"F0.wireOp",EDGE,"E223"),sQuery(id+"F0.wireOp",EDGE,"E224"),sQuery(id+"F0.wireOp",EDGE,"E225"),sQuery(id+"F0.wireOp",EDGE,"E226"),sQuery(id+"F0.wireOp",EDGE,"E227"),sQuery(id+"F0.wireOp",EDGE,"E228"),sQuery(id+"F0.wireOp",EDGE,"E229"),sQuery(id+"F0.wireOp",EDGE,"E230"),sQuery(id+"F0.wireOp",EDGE,"E231"),sQuery(id+"F0.wireOp",EDGE,"E232"),sQuery(id+"F0.wireOp",EDGE,"E233"),sQuery(id+"F0.wireOp",EDGE,"E234"),sQuery(id+"F0.wireOp",EDGE,"E235"),sQuery(id+"F0.wireOp",EDGE,"E236"),sQuery(id+"F0.wireOp",EDGE,"E237"),sQuery(id+"F0.wireOp",EDGE,"E238"),sQuery(id+"F0.wireOp",EDGE,"E239"),sQuery(id+"F0.wireOp",EDGE,"E240"),sQuery(id+"F0.wireOp",EDGE,"E241"),sQuery(id+"F0.wireOp",EDGE,"E242"),sQuery(id+"F0.wireOp",EDGE,"E243"),sQuery(id+"F0.wireOp",EDGE,"E244"),sQuery(id+"F0.wireOp",EDGE,"E245"),sQuery(id+"F0.wireOp",EDGE,"E246"),sQuery(id+"F0.wireOp",EDGE,"E247"),sQuery(id+"F0.wireOp",EDGE,"E248"),sQuery(id+"F0.wireOp",EDGE,"E249"),sQuery(id+"F0.wireOp",EDGE,"E250"),sQuery(id+"F0.wireOp",EDGE,"E251"),sQuery(id+"F0.wireOp",EDGE,"E252"),sQuery(id+"F0.wireOp",EDGE,"E253"),sQuery(id+"F0.wireOp",EDGE,"E254"),sQuery(id+"F0.wireOp",EDGE,"E255"),sQuery(id+"F0.wireOp",EDGE,"E256"),sQuery(id+"F0.wireOp",EDGE,"E257"),sQuery(id+"F0.wireOp",EDGE,"E258"),sQuery(id+"F0.wireOp",EDGE,"E259"),sQuery(id+"F0.wireOp",EDGE,"E260"),sQuery(id+"F0.wireOp",EDGE,"E261"),sQuery(id+"F0.wireOp",EDGE,"E262"),sQuery(id+"F0.wireOp",EDGE,"E263"),sQuery(id+"F0.wireOp",EDGE,"E264"),sQuery(id+"F0.wireOp",EDGE,"E265"),sQuery(id+"F0.wireOp",EDGE,"E266"),sQuery(id+"F0.wireOp",EDGE,"E267"),sQuery(id+"F0.wireOp",EDGE,"E268"),sQuery(id+"F0.wireOp",EDGE,"E269"),sQuery(id+"F0.wireOp",EDGE,"E270"),sQuery(id+"F0.wireOp",EDGE,"E271"),sQuery(id+"F0.wireOp",EDGE,"E272"),sQuery(id+"F0.wireOp",EDGE,"E273"),sQuery(id+"F0.wireOp",EDGE,"E274"),sQuery(id+"F0.wireOp",EDGE,"E275"),sQuery(id+"F0.wireOp",EDGE,"E276"),sQuery(id+"F0.wireOp",EDGE,"E277"),sQuery(id+"F0.wireOp",EDGE,"E278"),sQuery(id+"F0.wireOp",EDGE,"E279"),sQuery(id+"F0.wireOp",EDGE,"E280"),sQuery(id+"F0.wireOp",EDGE,"E281"),sQuery(id+"F0.wireOp",EDGE,"E282"),sQuery(id+"F0.wireOp",EDGE,"E283"),sQuery(id+"F0.wireOp",EDGE,"E284"),sQuery(id+"F0.wireOp",EDGE,"E285"),sQuery(id+"F0.wireOp",EDGE,"E286"),sQuery(id+"F0.wireOp",EDGE,"E287"),sQuery(id+"F0.wireOp",EDGE,"E288"),sQuery(id+"F0.wireOp",EDGE,"E289"),sQuery(id+"F0.wireOp",EDGE,"E290"),sQuery(id+"F0.wireOp",EDGE,"E291"),sQuery(id+"F0.wireOp",EDGE,"E292"),sQuery(id+"F0.wireOp",EDGE,"E293"),sQuery(id+"F0.wireOp",EDGE,"E294"),sQuery(id+"F0.wireOp",EDGE,"E295"),sQuery(id+"F0.wireOp",EDGE,"E296"),sQuery(id+"F0.wireOp",EDGE,"E297"),sQuery(id+"F0.wireOp",EDGE,"E298"),sQuery(id+"F0.wireOp",EDGE,"E299"),sQuery(id+"F0.wireOp",EDGE,"E300"),sQuery(id+"F0.wireOp",EDGE,"E301"),sQuery(id+"F0.wireOp",EDGE,"E302"),sQuery(id+"F0.wireOp",EDGE,"E303"),sQuery(id+"F0.wireOp",EDGE,"E304"),sQuery(id+"F0.wireOp",EDGE,"E305"),sQuery(id+"F0.wireOp",EDGE,"E306"),sQuery(id+"F0.wireOp",EDGE,"E307"),sQuery(id+"F0.wireOp",EDGE,"E308"),sQuery(id+"F0.wireOp",EDGE,"E309"),sQuery(id+"F0.wireOp",EDGE,"E310"),sQuery(id+"F0.wireOp",EDGE,"E311"),sQuery(id+"F0.wireOp",EDGE,"E312"),sQuery(id+"F0.wireOp",EDGE,"E313"),sQuery(id+"F0.wireOp",EDGE,"E314"),sQuery(id+"F0.wireOp",EDGE,"E315"),sQuery(id+"F0.wireOp",EDGE,"E316"),sQuery(id+"F0.wireOp",EDGE,"E317"),sQuery(id+"F0.wireOp",EDGE,"E318"),sQuery(id+"F0.wireOp",EDGE,"E319"),sQuery(id+"F0.wireOp",EDGE,"E320"),sQuery(id+"F0.wireOp",EDGE,"E321"),sQuery(id+"F0.wireOp",EDGE,"E322"),sQuery(id+"F0.wireOp",EDGE,"E323"),sQuery(id+"F0.wireOp",EDGE,"E324"),sQuery(id+"F0.wireOp",EDGE,"E325"),sQuery(id+"F0.wireOp",EDGE,"E326"),sQuery(id+"F0.wireOp",EDGE,"E327"),sQuery(id+"F0.wireOp",EDGE,"E328"),sQuery(id+"F0.wireOp",EDGE,"E329"),sQuery(id+"F0.wireOp",EDGE,"E330"),sQuery(id+"F0.wireOp",EDGE,"E331"),sQuery(id+"F0.wireOp",EDGE,"E332"),sQuery(id+"F0.wireOp",EDGE,"E333"),sQuery(id+"F0.wireOp",EDGE,"E334"),sQuery(id+"F0.wireOp",EDGE,"E335"),sQuery(id+"F0.wireOp",EDGE,"E336"),sQuery(id+"F0.wireOp",EDGE,"E337"),sQuery(id+"F0.wireOp",EDGE,"E338"),sQuery(id+"F0.wireOp",EDGE,"E339"),sQuery(id+"F0.wireOp",EDGE,"E340"),sQuery(id+"F0.wireOp",EDGE,"E341"),sQuery(id+"F0.wireOp",EDGE,"E342"),sQuery(id+"F0.wireOp",EDGE,"E343"),sQuery(id+"F0.wireOp",EDGE,"E344"),sQuery(id+"F0.wireOp",EDGE,"E345"),sQuery(id+"F0.wireOp",EDGE,"E346"),sQuery(id+"F0.wireOp",EDGE,"E347"),sQuery(id+"F0.wireOp",EDGE,"E348"),sQuery(id+"F0.wireOp",EDGE,"E349"),sQuery(id+"F0.wireOp",EDGE,"E350"),sQuery(id+"F0.wireOp",EDGE,"E351"),sQuery(id+"F0.wireOp",EDGE,"E352"),sQuery(id+"F0.wireOp",EDGE,"E353"),sQuery(id+"F0.wireOp",EDGE,"E354"),sQuery(id+"F0.wireOp",EDGE,"E355"),sQuery(id+"F0.wireOp",EDGE,"E356"),sQuery(id+"F0.wireOp",EDGE,"E357"),sQuery(id+"F0.wireOp",EDGE,"E358"),sQuery(id+"F0.wireOp",EDGE,"E359"),sQuery(id+"F0.wireOp",EDGE,"E360"),sQuery(id+"F0.wireOp",EDGE,"E361"),sQuery(id+"F0.wireOp",EDGE,"E362"),sQuery(id+"F0.wireOp",EDGE,"E363"),sQuery(id+"F0.wireOp",EDGE,"E364"),sQuery(id+"F0.wireOp",EDGE,"E365"),sQuery(id+"F0.wireOp",EDGE,"E366"),sQuery(id+"F0.wireOp",EDGE,"E367"),sQuery(id+"F0.wireOp",EDGE,"E368"),sQuery(id+"F0.wireOp",EDGE,"E369"),sQuery(id+"F0.wireOp",EDGE,"E370"),sQuery(id+"F0.wireOp",EDGE,"E371"),sQuery(id+"F0.wireOp",EDGE,"E372"),sQuery(id+"F0.wireOp",EDGE,"E373"),sQuery(id+"F0.wireOp",EDGE,"E374"),sQuery(id+"F0.wireOp",EDGE,"E375"),sQuery(id+"F0.wireOp",EDGE,"E376"),sQuery(id+"F0.wireOp",EDGE,"E377"),sQuery(id+"F0.wireOp",EDGE,"E378"),sQuery(id+"F0.wireOp",EDGE,"E379"),sQuery(id+"F0.wireOp",EDGE,"E642")])],"isStart":false});
            var sketch = newSketch(context, id + "F4", { "sketchPlane" : qUnion([Q0])});
            skLineSegment(sketch, "E644", {"start": v(22.83, 2.55) * mm, "end": v(22.83, -18.02) * mm});
            skSolve(sketch);
        }
        {
            var Q0;
            Q0 = qSketchRegion(id + "F4", true);
            var Q1;
            Q1=makeQuery(id+"F4.imprint","IMPRINT",FACE,{"disambiguationData":[TD([[makeQuery(id+"F4.imprint","IMPRINT",EDGE,{"derivedFrom":makeQuery(id+"F1.opExtrude","CAP_EDGE",EDGE,{"disambiguationData":[OSD([sQuery(id+"F0.wireOp",EDGE,"E174")])],"isStart":false})}),-1.0]])]});
            extrude(context, id + "F5", {"entities" : qUnion([Q0, Q1]), "operationType" : NewBodyOperationType.REMOVE, "oppositeDirection" : true, "depth" : 25 * mm});
        }
        {
            var Q0;
            Q0=makeQuery(id+"F1.opExtrude","CAP_FACE",FACE,{"disambiguationData":[OSD([sQuery(id+"F0.wireOp",EDGE,"E0"),sQuery(id+"F0.wireOp",EDGE,"E1"),sQuery(id+"F0.wireOp",EDGE,"E2"),sQuery(id+"F0.wireOp",EDGE,"E3"),sQuery(id+"F0.wireOp",EDGE,"E4"),sQuery(id+"F0.wireOp",EDGE,"E5"),sQuery(id+"F0.wireOp",EDGE,"E6"),sQuery(id+"F0.wireOp",EDGE,"E7"),sQuery(id+"F0.wireOp",EDGE,"E8"),sQuery(id+"F0.wireOp",EDGE,"E9"),sQuery(id+"F0.wireOp",EDGE,"E10"),sQuery(id+"F0.wireOp",EDGE,"E11"),sQuery(id+"F0.wireOp",EDGE,"E12"),sQuery(id+"F0.wireOp",EDGE,"E13"),sQuery(id+"F0.wireOp",EDGE,"E14"),sQuery(id+"F0.wireOp",EDGE,"E15"),sQuery(id+"F0.wireOp",EDGE,"E16"),sQuery(id+"F0.wireOp",EDGE,"E17"),sQuery(id+"F0.wireOp",EDGE,"E18"),sQuery(id+"F0.wireOp",EDGE,"E19"),sQuery(id+"F0.wireOp",EDGE,"E20"),sQuery(id+"F0.wireOp",EDGE,"E21"),sQuery(id+"F0.wireOp",EDGE,"E22"),sQuery(id+"F0.wireOp",EDGE,"E23"),sQuery(id+"F0.wireOp",EDGE,"E24"),sQuery(id+"F0.wireOp",EDGE,"E25"),sQuery(id+"F0.wireOp",EDGE,"E26"),sQuery(id+"F0.wireOp",EDGE,"E27"),sQuery(id+"F0.wireOp",EDGE,"E28"),sQuery(id+"F0.wireOp",EDGE,"E29"),sQuery(id+"F0.wireOp",EDGE,"E30"),sQuery(id+"F0.wireOp",EDGE,"E31"),sQuery(id+"F0.wireOp",EDGE,"E32"),sQuery(id+"F0.wireOp",EDGE,"E33"),sQuery(id+"F0.wireOp",EDGE,"E34"),sQuery(id+"F0.wireOp",EDGE,"E35"),sQuery(id+"F0.wireOp",EDGE,"E36"),sQuery(id+"F0.wireOp",EDGE,"E37"),sQuery(id+"F0.wireOp",EDGE,"E38"),sQuery(id+"F0.wireOp",EDGE,"E39"),sQuery(id+"F0.wireOp",EDGE,"E40"),sQuery(id+"F0.wireOp",EDGE,"E41"),sQuery(id+"F0.wireOp",EDGE,"E42"),sQuery(id+"F0.wireOp",EDGE,"E43"),sQuery(id+"F0.wireOp",EDGE,"E44"),sQuery(id+"F0.wireOp",EDGE,"E45"),sQuery(id+"F0.wireOp",EDGE,"E46"),sQuery(id+"F0.wireOp",EDGE,"E47"),sQuery(id+"F0.wireOp",EDGE,"E48"),sQuery(id+"F0.wireOp",EDGE,"E49"),sQuery(id+"F0.wireOp",EDGE,"E50"),sQuery(id+"F0.wireOp",EDGE,"E51"),sQuery(id+"F0.wireOp",EDGE,"E52"),sQuery(id+"F0.wireOp",EDGE,"E53"),sQuery(id+"F0.wireOp",EDGE,"E54"),sQuery(id+"F0.wireOp",EDGE,"E55"),sQuery(id+"F0.wireOp",EDGE,"E56"),sQuery(id+"F0.wireOp",EDGE,"E57"),sQuery(id+"F0.wireOp",EDGE,"E58"),sQuery(id+"F0.wireOp",EDGE,"E59"),sQuery(id+"F0.wireOp",EDGE,"E60"),sQuery(id+"F0.wireOp",EDGE,"E61"),sQuery(id+"F0.wireOp",EDGE,"E62"),sQuery(id+"F0.wireOp",EDGE,"E63"),sQuery(id+"F0.wireOp",EDGE,"E64"),sQuery(id+"F0.wireOp",EDGE,"E65"),sQuery(id+"F0.wireOp",EDGE,"E66"),sQuery(id+"F0.wireOp",EDGE,"E67"),sQuery(id+"F0.wireOp",EDGE,"E68"),sQuery(id+"F0.wireOp",EDGE,"E69"),sQuery(id+"F0.wireOp",EDGE,"E70"),sQuery(id+"F0.wireOp",EDGE,"E71"),sQuery(id+"F0.wireOp",EDGE,"E72"),sQuery(id+"F0.wireOp",EDGE,"E73"),sQuery(id+"F0.wireOp",EDGE,"E74"),sQuery(id+"F0.wireOp",EDGE,"E75"),sQuery(id+"F0.wireOp",EDGE,"E76"),sQuery(id+"F0.wireOp",EDGE,"E77"),sQuery(id+"F0.wireOp",EDGE,"E78"),sQuery(id+"F0.wireOp",EDGE,"E79"),sQuery(id+"F0.wireOp",EDGE,"E80"),sQuery(id+"F0.wireOp",EDGE,"E81"),sQuery(id+"F0.wireOp",EDGE,"E82"),sQuery(id+"F0.wireOp",EDGE,"E83"),sQuery(id+"F0.wireOp",EDGE,"E84"),sQuery(id+"F0.wireOp",EDGE,"E85"),sQuery(id+"F0.wireOp",EDGE,"E86"),sQuery(id+"F0.wireOp",EDGE,"E87"),sQuery(id+"F0.wireOp",EDGE,"E88"),sQuery(id+"F0.wireOp",EDGE,"E89"),sQuery(id+"F0.wireOp",EDGE,"E90"),sQuery(id+"F0.wireOp",EDGE,"E91"),sQuery(id+"F0.wireOp",EDGE,"E92"),sQuery(id+"F0.wireOp",EDGE,"E93"),sQuery(id+"F0.wireOp",EDGE,"E94"),sQuery(id+"F0.wireOp",EDGE,"E95"),sQuery(id+"F0.wireOp",EDGE,"E96"),sQuery(id+"F0.wireOp",EDGE,"E97"),sQuery(id+"F0.wireOp",EDGE,"E98"),sQuery(id+"F0.wireOp",EDGE,"E99"),sQuery(id+"F0.wireOp",EDGE,"E100"),sQuery(id+"F0.wireOp",EDGE,"E101"),sQuery(id+"F0.wireOp",EDGE,"E102"),sQuery(id+"F0.wireOp",EDGE,"E103"),sQuery(id+"F0.wireOp",EDGE,"E104"),sQuery(id+"F0.wireOp",EDGE,"E105"),sQuery(id+"F0.wireOp",EDGE,"E106"),sQuery(id+"F0.wireOp",EDGE,"E107"),sQuery(id+"F0.wireOp",EDGE,"E108"),sQuery(id+"F0.wireOp",EDGE,"E109"),sQuery(id+"F0.wireOp",EDGE,"E110"),sQuery(id+"F0.wireOp",EDGE,"E111"),sQuery(id+"F0.wireOp",EDGE,"E112"),sQuery(id+"F0.wireOp",EDGE,"E113"),sQuery(id+"F0.wireOp",EDGE,"E114"),sQuery(id+"F0.wireOp",EDGE,"E115"),sQuery(id+"F0.wireOp",EDGE,"E116"),sQuery(id+"F0.wireOp",EDGE,"E117"),sQuery(id+"F0.wireOp",EDGE,"E118"),sQuery(id+"F0.wireOp",EDGE,"E119"),sQuery(id+"F0.wireOp",EDGE,"E120"),sQuery(id+"F0.wireOp",EDGE,"E121"),sQuery(id+"F0.wireOp",EDGE,"E122"),sQuery(id+"F0.wireOp",EDGE,"E123"),sQuery(id+"F0.wireOp",EDGE,"E124"),sQuery(id+"F0.wireOp",EDGE,"E125"),sQuery(id+"F0.wireOp",EDGE,"E126"),sQuery(id+"F0.wireOp",EDGE,"E127"),sQuery(id+"F0.wireOp",EDGE,"E128"),sQuery(id+"F0.wireOp",EDGE,"E129"),sQuery(id+"F0.wireOp",EDGE,"E130"),sQuery(id+"F0.wireOp",EDGE,"E131"),sQuery(id+"F0.wireOp",EDGE,"E132"),sQuery(id+"F0.wireOp",EDGE,"E133"),sQuery(id+"F0.wireOp",EDGE,"E134"),sQuery(id+"F0.wireOp",EDGE,"E135"),sQuery(id+"F0.wireOp",EDGE,"E136"),sQuery(id+"F0.wireOp",EDGE,"E137"),sQuery(id+"F0.wireOp",EDGE,"E138"),sQuery(id+"F0.wireOp",EDGE,"E139"),sQuery(id+"F0.wireOp",EDGE,"E140"),sQuery(id+"F0.wireOp",EDGE,"E141"),sQuery(id+"F0.wireOp",EDGE,"E142"),sQuery(id+"F0.wireOp",EDGE,"E143"),sQuery(id+"F0.wireOp",EDGE,"E144"),sQuery(id+"F0.wireOp",EDGE,"E145"),sQuery(id+"F0.wireOp",EDGE,"E146"),sQuery(id+"F0.wireOp",EDGE,"E147"),sQuery(id+"F0.wireOp",EDGE,"E148"),sQuery(id+"F0.wireOp",EDGE,"E149"),sQuery(id+"F0.wireOp",EDGE,"E150"),sQuery(id+"F0.wireOp",EDGE,"E151"),sQuery(id+"F0.wireOp",EDGE,"E152"),sQuery(id+"F0.wireOp",EDGE,"E153"),sQuery(id+"F0.wireOp",EDGE,"E154"),sQuery(id+"F0.wireOp",EDGE,"E155"),sQuery(id+"F0.wireOp",EDGE,"E156"),sQuery(id+"F0.wireOp",EDGE,"E157"),sQuery(id+"F0.wireOp",EDGE,"E158"),sQuery(id+"F0.wireOp",EDGE,"E159"),sQuery(id+"F0.wireOp",EDGE,"E160"),sQuery(id+"F0.wireOp",EDGE,"E161"),sQuery(id+"F0.wireOp",EDGE,"E162"),sQuery(id+"F0.wireOp",EDGE,"E163"),sQuery(id+"F0.wireOp",EDGE,"E164"),sQuery(id+"F0.wireOp",EDGE,"E165"),sQuery(id+"F0.wireOp",EDGE,"E166"),sQuery(id+"F0.wireOp",EDGE,"E167"),sQuery(id+"F0.wireOp",EDGE,"E168"),sQuery(id+"F0.wireOp",EDGE,"E169"),sQuery(id+"F0.wireOp",EDGE,"E170"),sQuery(id+"F0.wireOp",EDGE,"E171"),sQuery(id+"F0.wireOp",EDGE,"E172"),sQuery(id+"F0.wireOp",EDGE,"E173"),sQuery(id+"F0.wireOp",EDGE,"E174"),sQuery(id+"F0.wireOp",EDGE,"E175"),sQuery(id+"F0.wireOp",EDGE,"E176"),sQuery(id+"F0.wireOp",EDGE,"E177"),sQuery(id+"F0.wireOp",EDGE,"E178"),sQuery(id+"F0.wireOp",EDGE,"E179"),sQuery(id+"F0.wireOp",EDGE,"E180"),sQuery(id+"F0.wireOp",EDGE,"E181"),sQuery(id+"F0.wireOp",EDGE,"E182"),sQuery(id+"F0.wireOp",EDGE,"E183"),sQuery(id+"F0.wireOp",EDGE,"E184"),sQuery(id+"F0.wireOp",EDGE,"E185"),sQuery(id+"F0.wireOp",EDGE,"E186"),sQuery(id+"F0.wireOp",EDGE,"E187"),sQuery(id+"F0.wireOp",EDGE,"E188"),sQuery(id+"F0.wireOp",EDGE,"E189"),sQuery(id+"F0.wireOp",EDGE,"E190"),sQuery(id+"F0.wireOp",EDGE,"E191"),sQuery(id+"F0.wireOp",EDGE,"E192"),sQuery(id+"F0.wireOp",EDGE,"E193"),sQuery(id+"F0.wireOp",EDGE,"E194"),sQuery(id+"F0.wireOp",EDGE,"E195"),sQuery(id+"F0.wireOp",EDGE,"E196"),sQuery(id+"F0.wireOp",EDGE,"E197"),sQuery(id+"F0.wireOp",EDGE,"E198"),sQuery(id+"F0.wireOp",EDGE,"E199"),sQuery(id+"F0.wireOp",EDGE,"E200"),sQuery(id+"F0.wireOp",EDGE,"E201"),sQuery(id+"F0.wireOp",EDGE,"E202"),sQuery(id+"F0.wireOp",EDGE,"E203"),sQuery(id+"F0.wireOp",EDGE,"E204"),sQuery(id+"F0.wireOp",EDGE,"E205"),sQuery(id+"F0.wireOp",EDGE,"E206"),sQuery(id+"F0.wireOp",EDGE,"E207"),sQuery(id+"F0.wireOp",EDGE,"E208"),sQuery(id+"F0.wireOp",EDGE,"E209"),sQuery(id+"F0.wireOp",EDGE,"E210"),sQuery(id+"F0.wireOp",EDGE,"E211"),sQuery(id+"F0.wireOp",EDGE,"E212"),sQuery(id+"F0.wireOp",EDGE,"E213"),sQuery(id+"F0.wireOp",EDGE,"E214"),sQuery(id+"F0.wireOp",EDGE,"E215"),sQuery(id+"F0.wireOp",EDGE,"E216"),sQuery(id+"F0.wireOp",EDGE,"E217"),sQuery(id+"F0.wireOp",EDGE,"E218"),sQuery(id+"F0.wireOp",EDGE,"E219"),sQuery(id+"F0.wireOp",EDGE,"E220"),sQuery(id+"F0.wireOp",EDGE,"E221"),sQuery(id+"F0.wireOp",EDGE,"E222"),sQuery(id+"F0.wireOp",EDGE,"E223"),sQuery(id+"F0.wireOp",EDGE,"E224"),sQuery(id+"F0.wireOp",EDGE,"E225"),sQuery(id+"F0.wireOp",EDGE,"E226"),sQuery(id+"F0.wireOp",EDGE,"E227"),sQuery(id+"F0.wireOp",EDGE,"E228"),sQuery(id+"F0.wireOp",EDGE,"E229"),sQuery(id+"F0.wireOp",EDGE,"E230"),sQuery(id+"F0.wireOp",EDGE,"E231"),sQuery(id+"F0.wireOp",EDGE,"E232"),sQuery(id+"F0.wireOp",EDGE,"E233"),sQuery(id+"F0.wireOp",EDGE,"E234"),sQuery(id+"F0.wireOp",EDGE,"E235"),sQuery(id+"F0.wireOp",EDGE,"E236"),sQuery(id+"F0.wireOp",EDGE,"E237"),sQuery(id+"F0.wireOp",EDGE,"E238"),sQuery(id+"F0.wireOp",EDGE,"E239"),sQuery(id+"F0.wireOp",EDGE,"E240"),sQuery(id+"F0.wireOp",EDGE,"E241"),sQuery(id+"F0.wireOp",EDGE,"E242"),sQuery(id+"F0.wireOp",EDGE,"E243"),sQuery(id+"F0.wireOp",EDGE,"E244"),sQuery(id+"F0.wireOp",EDGE,"E245"),sQuery(id+"F0.wireOp",EDGE,"E246"),sQuery(id+"F0.wireOp",EDGE,"E247"),sQuery(id+"F0.wireOp",EDGE,"E248"),sQuery(id+"F0.wireOp",EDGE,"E249"),sQuery(id+"F0.wireOp",EDGE,"E250"),sQuery(id+"F0.wireOp",EDGE,"E251"),sQuery(id+"F0.wireOp",EDGE,"E252"),sQuery(id+"F0.wireOp",EDGE,"E253"),sQuery(id+"F0.wireOp",EDGE,"E254"),sQuery(id+"F0.wireOp",EDGE,"E255"),sQuery(id+"F0.wireOp",EDGE,"E256"),sQuery(id+"F0.wireOp",EDGE,"E257"),sQuery(id+"F0.wireOp",EDGE,"E258"),sQuery(id+"F0.wireOp",EDGE,"E259"),sQuery(id+"F0.wireOp",EDGE,"E260"),sQuery(id+"F0.wireOp",EDGE,"E261"),sQuery(id+"F0.wireOp",EDGE,"E262"),sQuery(id+"F0.wireOp",EDGE,"E263"),sQuery(id+"F0.wireOp",EDGE,"E264"),sQuery(id+"F0.wireOp",EDGE,"E265"),sQuery(id+"F0.wireOp",EDGE,"E266"),sQuery(id+"F0.wireOp",EDGE,"E267"),sQuery(id+"F0.wireOp",EDGE,"E268"),sQuery(id+"F0.wireOp",EDGE,"E269"),sQuery(id+"F0.wireOp",EDGE,"E270"),sQuery(id+"F0.wireOp",EDGE,"E271"),sQuery(id+"F0.wireOp",EDGE,"E272"),sQuery(id+"F0.wireOp",EDGE,"E273"),sQuery(id+"F0.wireOp",EDGE,"E274"),sQuery(id+"F0.wireOp",EDGE,"E275"),sQuery(id+"F0.wireOp",EDGE,"E276"),sQuery(id+"F0.wireOp",EDGE,"E277"),sQuery(id+"F0.wireOp",EDGE,"E278"),sQuery(id+"F0.wireOp",EDGE,"E279"),sQuery(id+"F0.wireOp",EDGE,"E280"),sQuery(id+"F0.wireOp",EDGE,"E281"),sQuery(id+"F0.wireOp",EDGE,"E282"),sQuery(id+"F0.wireOp",EDGE,"E283"),sQuery(id+"F0.wireOp",EDGE,"E284"),sQuery(id+"F0.wireOp",EDGE,"E285"),sQuery(id+"F0.wireOp",EDGE,"E286"),sQuery(id+"F0.wireOp",EDGE,"E287"),sQuery(id+"F0.wireOp",EDGE,"E288"),sQuery(id+"F0.wireOp",EDGE,"E289"),sQuery(id+"F0.wireOp",EDGE,"E290"),sQuery(id+"F0.wireOp",EDGE,"E291"),sQuery(id+"F0.wireOp",EDGE,"E292"),sQuery(id+"F0.wireOp",EDGE,"E293"),sQuery(id+"F0.wireOp",EDGE,"E294"),sQuery(id+"F0.wireOp",EDGE,"E295"),sQuery(id+"F0.wireOp",EDGE,"E296"),sQuery(id+"F0.wireOp",EDGE,"E297"),sQuery(id+"F0.wireOp",EDGE,"E298"),sQuery(id+"F0.wireOp",EDGE,"E299"),sQuery(id+"F0.wireOp",EDGE,"E300"),sQuery(id+"F0.wireOp",EDGE,"E301"),sQuery(id+"F0.wireOp",EDGE,"E302"),sQuery(id+"F0.wireOp",EDGE,"E303"),sQuery(id+"F0.wireOp",EDGE,"E304"),sQuery(id+"F0.wireOp",EDGE,"E305"),sQuery(id+"F0.wireOp",EDGE,"E306"),sQuery(id+"F0.wireOp",EDGE,"E307"),sQuery(id+"F0.wireOp",EDGE,"E308"),sQuery(id+"F0.wireOp",EDGE,"E309"),sQuery(id+"F0.wireOp",EDGE,"E310"),sQuery(id+"F0.wireOp",EDGE,"E311"),sQuery(id+"F0.wireOp",EDGE,"E312"),sQuery(id+"F0.wireOp",EDGE,"E313"),sQuery(id+"F0.wireOp",EDGE,"E314"),sQuery(id+"F0.wireOp",EDGE,"E315"),sQuery(id+"F0.wireOp",EDGE,"E316"),sQuery(id+"F0.wireOp",EDGE,"E317"),sQuery(id+"F0.wireOp",EDGE,"E318"),sQuery(id+"F0.wireOp",EDGE,"E319"),sQuery(id+"F0.wireOp",EDGE,"E320"),sQuery(id+"F0.wireOp",EDGE,"E321"),sQuery(id+"F0.wireOp",EDGE,"E322"),sQuery(id+"F0.wireOp",EDGE,"E323"),sQuery(id+"F0.wireOp",EDGE,"E324"),sQuery(id+"F0.wireOp",EDGE,"E325"),sQuery(id+"F0.wireOp",EDGE,"E326"),sQuery(id+"F0.wireOp",EDGE,"E327"),sQuery(id+"F0.wireOp",EDGE,"E328"),sQuery(id+"F0.wireOp",EDGE,"E329"),sQuery(id+"F0.wireOp",EDGE,"E330"),sQuery(id+"F0.wireOp",EDGE,"E331"),sQuery(id+"F0.wireOp",EDGE,"E332"),sQuery(id+"F0.wireOp",EDGE,"E333"),sQuery(id+"F0.wireOp",EDGE,"E334"),sQuery(id+"F0.wireOp",EDGE,"E335"),sQuery(id+"F0.wireOp",EDGE,"E336"),sQuery(id+"F0.wireOp",EDGE,"E337"),sQuery(id+"F0.wireOp",EDGE,"E338"),sQuery(id+"F0.wireOp",EDGE,"E339"),sQuery(id+"F0.wireOp",EDGE,"E340"),sQuery(id+"F0.wireOp",EDGE,"E341"),sQuery(id+"F0.wireOp",EDGE,"E342"),sQuery(id+"F0.wireOp",EDGE,"E343"),sQuery(id+"F0.wireOp",EDGE,"E344"),sQuery(id+"F0.wireOp",EDGE,"E345"),sQuery(id+"F0.wireOp",EDGE,"E346"),sQuery(id+"F0.wireOp",EDGE,"E347"),sQuery(id+"F0.wireOp",EDGE,"E348"),sQuery(id+"F0.wireOp",EDGE,"E349"),sQuery(id+"F0.wireOp",EDGE,"E350"),sQuery(id+"F0.wireOp",EDGE,"E351"),sQuery(id+"F0.wireOp",EDGE,"E352"),sQuery(id+"F0.wireOp",EDGE,"E353"),sQuery(id+"F0.wireOp",EDGE,"E354"),sQuery(id+"F0.wireOp",EDGE,"E355"),sQuery(id+"F0.wireOp",EDGE,"E356"),sQuery(id+"F0.wireOp",EDGE,"E357"),sQuery(id+"F0.wireOp",EDGE,"E358"),sQuery(id+"F0.wireOp",EDGE,"E359"),sQuery(id+"F0.wireOp",EDGE,"E360"),sQuery(id+"F0.wireOp",EDGE,"E361"),sQuery(id+"F0.wireOp",EDGE,"E362"),sQuery(id+"F0.wireOp",EDGE,"E363"),sQuery(id+"F0.wireOp",EDGE,"E364"),sQuery(id+"F0.wireOp",EDGE,"E365"),sQuery(id+"F0.wireOp",EDGE,"E366"),sQuery(id+"F0.wireOp",EDGE,"E367"),sQuery(id+"F0.wireOp",EDGE,"E368"),sQuery(id+"F0.wireOp",EDGE,"E369"),sQuery(id+"F0.wireOp",EDGE,"E370"),sQuery(id+"F0.wireOp",EDGE,"E371"),sQuery(id+"F0.wireOp",EDGE,"E372"),sQuery(id+"F0.wireOp",EDGE,"E373"),sQuery(id+"F0.wireOp",EDGE,"E374"),sQuery(id+"F0.wireOp",EDGE,"E375"),sQuery(id+"F0.wireOp",EDGE,"E376"),sQuery(id+"F0.wireOp",EDGE,"E377"),sQuery(id+"F0.wireOp",EDGE,"E378"),sQuery(id+"F0.wireOp",EDGE,"E379"),sQuery(id+"F0.wireOp",EDGE,"E642")])],"isStart":false});
            extrude(context, id + "F6", {"entities" : qUnion([Q0]), "operationType" : NewBodyOperationType.REMOVE, "oppositeDirection" : true, "depth" : 15 * mm});
        }
    });
